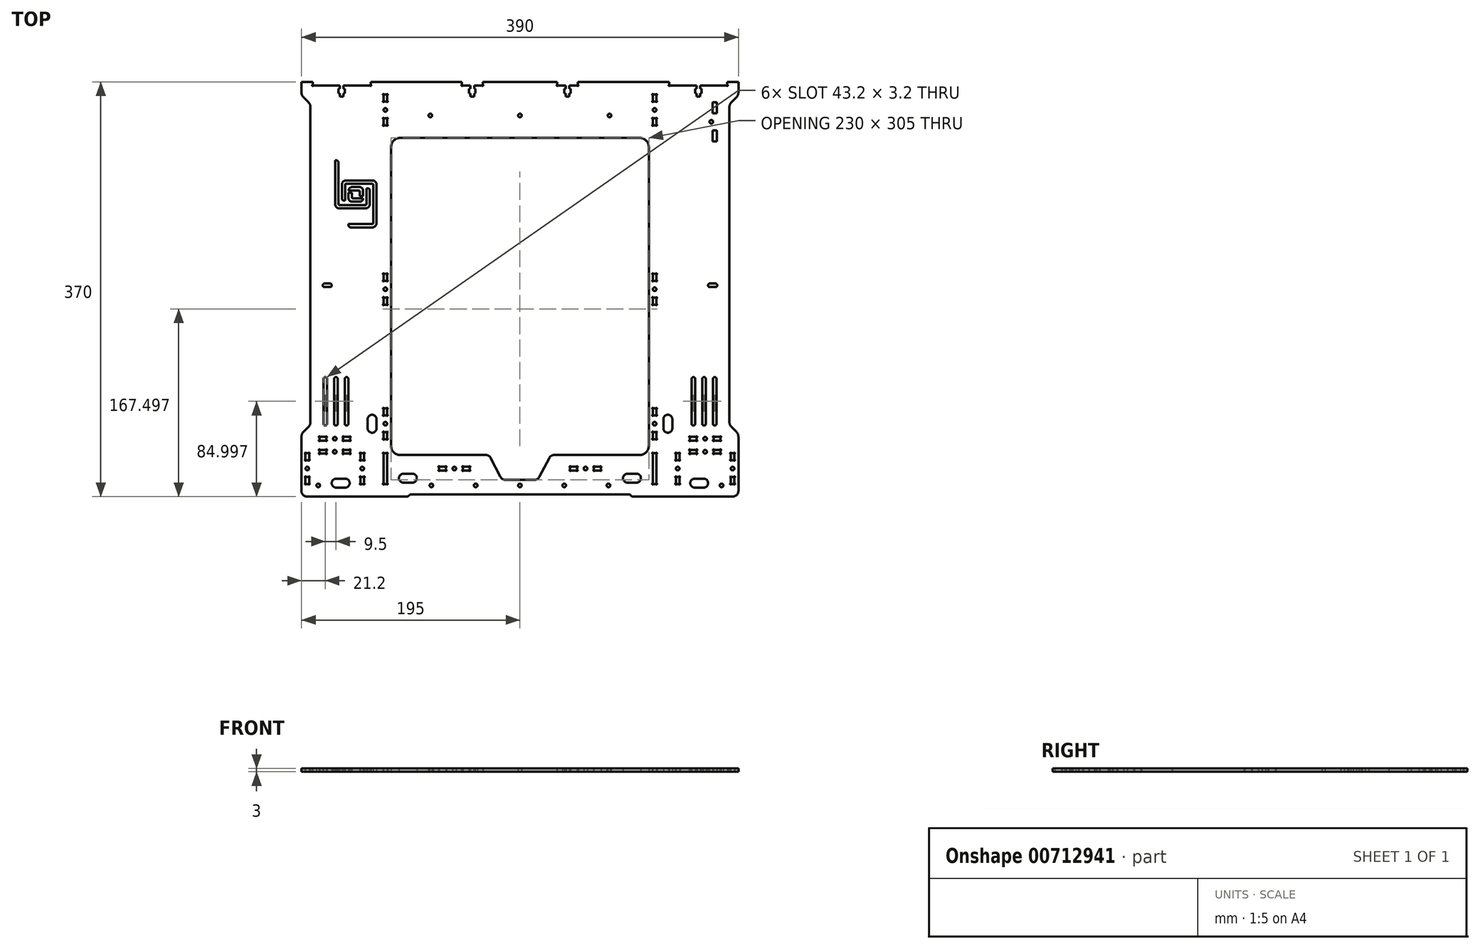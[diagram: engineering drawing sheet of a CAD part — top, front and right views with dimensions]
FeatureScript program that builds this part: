
annotation { "Feature Type Name" : "Feature", "Feature Type Description" : "" }
export const myFeature = defineFeature(function(context is Context, id is Id, definition is map)
    precondition{}
    {
        {
            var Q0;
            Q0=qCreatedBy(makeId("Top.planeOp"),FACE);
            var sketch = newSketch(context, id + "F0", { "sketchPlane" : qUnion([Q0])});
            skCircle(sketch, "E0", {"center": v(-180, -171.15) * mm, "radius": 1.6 * mm});
            skCircle(sketch, "E1", {"center": v(0, 158.85) * mm, "radius": 1.6 * mm});
            skLineSegment(sketch, "E2", {"start": v(-156, -165.15) * mm, "end": v(-164, -165.15) * mm});
            skArc(sketch, "E3", {"start": v(-156, -173.15) * mm, "mid": v(-152, -169.15) * mm, "end": v(-156, -165.15) * mm});
            skLineSegment(sketch, "E4", {"start": v(-164, -173.15) * mm, "end": v(-156, -173.15) * mm});
            skArc(sketch, "E5", {"start": v(-164, -165.15) * mm, "mid": v(-168, -169.15) * mm, "end": v(-164, -173.15) * mm});
            skLineSegment(sketch, "E6", {"start": v(156, -173.15) * mm, "end": v(164, -173.15) * mm});
            skArc(sketch, "E7", {"start": v(156, -165.15) * mm, "mid": v(152, -169.15) * mm, "end": v(156, -173.15) * mm});
            skLineSegment(sketch, "E8", {"start": v(164, -165.15) * mm, "end": v(156, -165.15) * mm});
            skArc(sketch, "E9", {"start": v(164, -173.15) * mm, "mid": v(168, -169.15) * mm, "end": v(164, -165.15) * mm});
            skLineSegment(sketch, "E10", {"start": v(-165.9, -76.15) * mm, "end": v(-165.9, -116.15) * mm});
            skArc(sketch, "E11", {"start": v(-162.7, -76.15) * mm, "mid": v(-164.3, -74.55) * mm, "end": v(-165.9, -76.15) * mm});
            skLineSegment(sketch, "E12", {"start": v(-162.7, -116.15) * mm, "end": v(-162.7, -76.15) * mm});
            skArc(sketch, "E13", {"start": v(-165.9, -116.15) * mm, "mid": v(-164.3, -117.75) * mm, "end": v(-162.7, -116.15) * mm});
            skLineSegment(sketch, "E14", {"start": v(-156.4, -76.15) * mm, "end": v(-156.4, -116.15) * mm});
            skArc(sketch, "E15", {"start": v(-153.2, -76.15) * mm, "mid": v(-154.8, -74.55) * mm, "end": v(-156.4, -76.15) * mm});
            skLineSegment(sketch, "E16", {"start": v(-153.2, -116.15) * mm, "end": v(-153.2, -76.15) * mm});
            skArc(sketch, "E17", {"start": v(-156.4, -116.15) * mm, "mid": v(-154.8, -117.75) * mm, "end": v(-153.2, -116.15) * mm});
            skLineSegment(sketch, "E18", {"start": v(-175.4, -76.15) * mm, "end": v(-175.4, -116.15) * mm});
            skArc(sketch, "E19", {"start": v(-172.2, -76.15) * mm, "mid": v(-173.8, -74.55) * mm, "end": v(-175.4, -76.15) * mm});
            skLineSegment(sketch, "E20", {"start": v(-172.2, -116.15) * mm, "end": v(-172.2, -76.15) * mm});
            skArc(sketch, "E21", {"start": v(-175.4, -116.15) * mm, "mid": v(-173.8, -117.75) * mm, "end": v(-172.2, -116.15) * mm});
            skCircle(sketch, "E22", {"center": v(170.82, 153.25) * mm, "radius": 1.6 * mm});
            skCircle(sketch, "E23", {"center": v(165.3, -141.15) * mm, "radius": 1.6 * mm});
            skLineSegment(sketch, "E24", {"start": v(-157.8, -140.37) * mm, "end": v(-157.8, -141.94) * mm});
            skArc(sketch, "E25", {"start": v(-157.8, -140.37) * mm, "mid": v(-157.87, -140.12) * mm, "end": v(-158.05, -139.94) * mm});
            skArc(sketch, "E26", {"start": v(-157.37, -139.25) * mm, "mid": v(-158.15, -139.15) * mm, "end": v(-158.05, -139.94) * mm});
            skArc(sketch, "E27", {"start": v(-157.37, -139.25) * mm, "mid": v(-157.18, -139.44) * mm, "end": v(-156.93, -139.5) * mm});
            skLineSegment(sketch, "E28", {"start": v(-152.47, -139.5) * mm, "end": v(-156.93, -139.5) * mm});
            skArc(sketch, "E29", {"start": v(-152.47, -139.5) * mm, "mid": v(-152.22, -139.44) * mm, "end": v(-152.03, -139.25) * mm});
            skArc(sketch, "E30", {"start": v(-151.35, -139.94) * mm, "mid": v(-151.25, -139.15) * mm, "end": v(-152.03, -139.25) * mm});
            skArc(sketch, "E31", {"start": v(-151.35, -139.94) * mm, "mid": v(-151.53, -140.12) * mm, "end": v(-151.6, -140.37) * mm});
            skLineSegment(sketch, "E32", {"start": v(-151.6, -141.94) * mm, "end": v(-151.6, -140.37) * mm});
            skArc(sketch, "E33", {"start": v(-151.6, -141.94) * mm, "mid": v(-151.53, -142.19) * mm, "end": v(-151.35, -142.37) * mm});
            skArc(sketch, "E34", {"start": v(-152.03, -143.05) * mm, "mid": v(-151.25, -143.16) * mm, "end": v(-151.35, -142.37) * mm});
            skArc(sketch, "E35", {"start": v(-152.03, -143.05) * mm, "mid": v(-152.22, -142.87) * mm, "end": v(-152.47, -142.8) * mm});
            skLineSegment(sketch, "E36", {"start": v(-156.93, -142.8) * mm, "end": v(-152.47, -142.8) * mm});
            skArc(sketch, "E37", {"start": v(-156.93, -142.8) * mm, "mid": v(-157.18, -142.87) * mm, "end": v(-157.37, -143.05) * mm});
            skArc(sketch, "E38", {"start": v(-158.05, -142.37) * mm, "mid": v(-158.15, -143.16) * mm, "end": v(-157.37, -143.05) * mm});
            skArc(sketch, "E39", {"start": v(-158.05, -142.37) * mm, "mid": v(-157.87, -142.19) * mm, "end": v(-157.8, -141.94) * mm});
            skLineSegment(sketch, "E40", {"start": v(-179, -140.37) * mm, "end": v(-179, -141.94) * mm});
            skArc(sketch, "E41", {"start": v(-179, -140.37) * mm, "mid": v(-179.07, -140.12) * mm, "end": v(-179.25, -139.94) * mm});
            skArc(sketch, "E42", {"start": v(-178.57, -139.25) * mm, "mid": v(-179.35, -139.15) * mm, "end": v(-179.25, -139.94) * mm});
            skArc(sketch, "E43", {"start": v(-178.57, -139.25) * mm, "mid": v(-178.38, -139.44) * mm, "end": v(-178.13, -139.5) * mm});
            skLineSegment(sketch, "E44", {"start": v(-173.67, -139.5) * mm, "end": v(-178.13, -139.5) * mm});
            skArc(sketch, "E45", {"start": v(-173.67, -139.5) * mm, "mid": v(-173.42, -139.44) * mm, "end": v(-173.23, -139.25) * mm});
            skArc(sketch, "E46", {"start": v(-172.55, -139.94) * mm, "mid": v(-172.45, -139.15) * mm, "end": v(-173.23, -139.25) * mm});
            skArc(sketch, "E47", {"start": v(-172.55, -139.94) * mm, "mid": v(-172.73, -140.12) * mm, "end": v(-172.8, -140.37) * mm});
            skLineSegment(sketch, "E48", {"start": v(-172.8, -141.94) * mm, "end": v(-172.8, -140.37) * mm});
            skArc(sketch, "E49", {"start": v(-172.8, -141.94) * mm, "mid": v(-172.73, -142.19) * mm, "end": v(-172.55, -142.37) * mm});
            skArc(sketch, "E50", {"start": v(-173.23, -143.05) * mm, "mid": v(-172.45, -143.16) * mm, "end": v(-172.55, -142.37) * mm});
            skArc(sketch, "E51", {"start": v(-173.23, -143.05) * mm, "mid": v(-173.42, -142.87) * mm, "end": v(-173.67, -142.8) * mm});
            skLineSegment(sketch, "E52", {"start": v(-178.13, -142.8) * mm, "end": v(-173.67, -142.8) * mm});
            skArc(sketch, "E53", {"start": v(-178.13, -142.8) * mm, "mid": v(-178.38, -142.87) * mm, "end": v(-178.57, -143.05) * mm});
            skArc(sketch, "E54", {"start": v(-179.25, -142.37) * mm, "mid": v(-179.35, -143.16) * mm, "end": v(-178.57, -143.05) * mm});
            skArc(sketch, "E55", {"start": v(-179.25, -142.37) * mm, "mid": v(-179.07, -142.19) * mm, "end": v(-179, -141.94) * mm});
            skLineSegment(sketch, "E56", {"start": v(-96, -160.75) * mm, "end": v(-104, -160.75) * mm});
            skArc(sketch, "E57", {"start": v(-96, -168.75) * mm, "mid": v(-92, -164.75) * mm, "end": v(-96, -160.75) * mm});
            skLineSegment(sketch, "E58", {"start": v(-104, -168.75) * mm, "end": v(-96, -168.75) * mm});
            skArc(sketch, "E59", {"start": v(-104, -160.75) * mm, "mid": v(-108, -164.75) * mm, "end": v(-104, -168.75) * mm});
            skLineSegment(sketch, "E60", {"start": v(104, -160.75) * mm, "end": v(96, -160.75) * mm});
            skArc(sketch, "E61", {"start": v(104, -168.75) * mm, "mid": v(108, -164.75) * mm, "end": v(104, -160.75) * mm});
            skLineSegment(sketch, "E62", {"start": v(96, -168.75) * mm, "end": v(104, -168.75) * mm});
            skArc(sketch, "E63", {"start": v(96, -160.75) * mm, "mid": v(92, -164.75) * mm, "end": v(96, -168.75) * mm});
            skCircle(sketch, "E64", {"center": v(-79.02, -171.15) * mm, "radius": 1.6 * mm});
            skCircle(sketch, "E65", {"center": v(39.5, -171.15) * mm, "radius": 1.6 * mm});
            skCircle(sketch, "E66", {"center": v(58.53, -156.15) * mm, "radius": 1.6 * mm});
            skLineSegment(sketch, "E67", {"start": v(-51.03, -155.37) * mm, "end": v(-51.03, -156.94) * mm});
            skArc(sketch, "E68", {"start": v(-51.03, -155.37) * mm, "mid": v(-51.1, -155.12) * mm, "end": v(-51.28, -154.94) * mm});
            skArc(sketch, "E69", {"start": v(-50.6, -154.25) * mm, "mid": v(-51.38, -154.15) * mm, "end": v(-51.28, -154.94) * mm});
            skArc(sketch, "E70", {"start": v(-50.6, -154.25) * mm, "mid": v(-50.4, -154.44) * mm, "end": v(-50.16, -154.5) * mm});
            skLineSegment(sketch, "E71", {"start": v(-45.7, -154.5) * mm, "end": v(-50.16, -154.5) * mm});
            skArc(sketch, "E72", {"start": v(-45.7, -154.5) * mm, "mid": v(-45.44, -154.44) * mm, "end": v(-45.26, -154.25) * mm});
            skArc(sketch, "E73", {"start": v(-44.58, -154.94) * mm, "mid": v(-44.47, -154.15) * mm, "end": v(-45.26, -154.25) * mm});
            skArc(sketch, "E74", {"start": v(-44.58, -154.94) * mm, "mid": v(-44.76, -155.12) * mm, "end": v(-44.83, -155.37) * mm});
            skLineSegment(sketch, "E75", {"start": v(-44.83, -156.94) * mm, "end": v(-44.83, -155.37) * mm});
            skArc(sketch, "E76", {"start": v(-44.83, -156.94) * mm, "mid": v(-44.76, -157.19) * mm, "end": v(-44.58, -157.37) * mm});
            skArc(sketch, "E77", {"start": v(-45.26, -158.05) * mm, "mid": v(-44.47, -158.16) * mm, "end": v(-44.58, -157.37) * mm});
            skArc(sketch, "E78", {"start": v(-45.26, -158.05) * mm, "mid": v(-45.44, -157.87) * mm, "end": v(-45.7, -157.8) * mm});
            skLineSegment(sketch, "E79", {"start": v(-50.16, -157.8) * mm, "end": v(-45.7, -157.8) * mm});
            skArc(sketch, "E80", {"start": v(-50.16, -157.8) * mm, "mid": v(-50.4, -157.87) * mm, "end": v(-50.6, -158.05) * mm});
            skArc(sketch, "E81", {"start": v(-51.28, -157.37) * mm, "mid": v(-51.38, -158.16) * mm, "end": v(-50.6, -158.05) * mm});
            skArc(sketch, "E82", {"start": v(-51.28, -157.37) * mm, "mid": v(-51.1, -157.19) * mm, "end": v(-51.03, -156.94) * mm});
            skLineSegment(sketch, "E83", {"start": v(-72.23, -155.37) * mm, "end": v(-72.23, -156.94) * mm});
            skArc(sketch, "E84", {"start": v(-72.23, -155.37) * mm, "mid": v(-72.3, -155.12) * mm, "end": v(-72.48, -154.94) * mm});
            skArc(sketch, "E85", {"start": v(-71.8, -154.25) * mm, "mid": v(-72.58, -154.15) * mm, "end": v(-72.48, -154.94) * mm});
            skArc(sketch, "E86", {"start": v(-71.8, -154.25) * mm, "mid": v(-71.6, -154.44) * mm, "end": v(-71.36, -154.5) * mm});
            skLineSegment(sketch, "E87", {"start": v(-66.9, -154.5) * mm, "end": v(-71.36, -154.5) * mm});
            skArc(sketch, "E88", {"start": v(-66.9, -154.5) * mm, "mid": v(-66.64, -154.44) * mm, "end": v(-66.46, -154.25) * mm});
            skArc(sketch, "E89", {"start": v(-65.78, -154.94) * mm, "mid": v(-65.67, -154.15) * mm, "end": v(-66.46, -154.25) * mm});
            skArc(sketch, "E90", {"start": v(-65.78, -154.94) * mm, "mid": v(-65.96, -155.12) * mm, "end": v(-66.03, -155.37) * mm});
            skLineSegment(sketch, "E91", {"start": v(-66.03, -156.94) * mm, "end": v(-66.03, -155.37) * mm});
            skArc(sketch, "E92", {"start": v(-66.03, -156.94) * mm, "mid": v(-65.96, -157.19) * mm, "end": v(-65.78, -157.37) * mm});
            skArc(sketch, "E93", {"start": v(-66.46, -158.05) * mm, "mid": v(-65.67, -158.16) * mm, "end": v(-65.78, -157.37) * mm});
            skArc(sketch, "E94", {"start": v(-66.46, -158.05) * mm, "mid": v(-66.64, -157.87) * mm, "end": v(-66.9, -157.8) * mm});
            skLineSegment(sketch, "E95", {"start": v(-71.36, -157.8) * mm, "end": v(-66.9, -157.8) * mm});
            skArc(sketch, "E96", {"start": v(-71.36, -157.8) * mm, "mid": v(-71.6, -157.87) * mm, "end": v(-71.8, -158.05) * mm});
            skArc(sketch, "E97", {"start": v(-72.48, -157.37) * mm, "mid": v(-72.58, -158.16) * mm, "end": v(-71.8, -158.05) * mm});
            skArc(sketch, "E98", {"start": v(-72.48, -157.37) * mm, "mid": v(-72.3, -157.19) * mm, "end": v(-72.23, -156.94) * mm});
            skCircle(sketch, "E99", {"center": v(189.82, -156.15) * mm, "radius": 1.6 * mm});
            skCircle(sketch, "E100", {"center": v(140.78, -156.15) * mm, "radius": 1.6 * mm});
            skCircle(sketch, "E101", {"center": v(120.17, 3.85) * mm, "radius": 1.6 * mm});
            skCircle(sketch, "E102", {"center": v(-120.18, 163.85) * mm, "radius": 1.6 * mm});
            skCircle(sketch, "E103", {"center": v(-120.17, -116.15) * mm, "radius": 1.6 * mm});
            skCircle(sketch, "E104", {"center": v(-165.3, -129.5) * mm, "radius": 1.6 * mm});
            skArc(sketch, "E105", {"start": v(188.17, -143.32) * mm, "mid": v(188.1, -143.07) * mm, "end": v(187.92, -142.89) * mm});
            skArc(sketch, "E106", {"start": v(188.6, -142.2) * mm, "mid": v(187.82, -142.1) * mm, "end": v(187.92, -142.89) * mm});
            skArc(sketch, "E107", {"start": v(188.6, -142.2) * mm, "mid": v(188.79, -142.39) * mm, "end": v(189.04, -142.45) * mm});
            skLineSegment(sketch, "E108", {"start": v(190.6, -142.45) * mm, "end": v(189.04, -142.45) * mm});
            skArc(sketch, "E109", {"start": v(190.6, -142.45) * mm, "mid": v(190.85, -142.39) * mm, "end": v(191.04, -142.2) * mm});
            skArc(sketch, "E110", {"start": v(191.72, -142.89) * mm, "mid": v(191.82, -142.1) * mm, "end": v(191.04, -142.2) * mm});
            skArc(sketch, "E111", {"start": v(191.72, -142.89) * mm, "mid": v(191.54, -143.07) * mm, "end": v(191.47, -143.32) * mm});
            skLineSegment(sketch, "E112", {"start": v(191.47, -147.79) * mm, "end": v(191.47, -143.32) * mm});
            skArc(sketch, "E113", {"start": v(191.47, -147.79) * mm, "mid": v(191.54, -148.04) * mm, "end": v(191.72, -148.22) * mm});
            skArc(sketch, "E114", {"start": v(191.04, -148.9) * mm, "mid": v(191.82, -149) * mm, "end": v(191.72, -148.22) * mm});
            skArc(sketch, "E115", {"start": v(191.04, -148.9) * mm, "mid": v(190.85, -148.72) * mm, "end": v(190.6, -148.65) * mm});
            skLineSegment(sketch, "E116", {"start": v(189.04, -148.65) * mm, "end": v(190.6, -148.65) * mm});
            skArc(sketch, "E117", {"start": v(189.04, -148.65) * mm, "mid": v(188.79, -148.72) * mm, "end": v(188.6, -148.9) * mm});
            skArc(sketch, "E118", {"start": v(187.92, -148.22) * mm, "mid": v(187.82, -149) * mm, "end": v(188.6, -148.9) * mm});
            skArc(sketch, "E119", {"start": v(187.92, -148.22) * mm, "mid": v(188.1, -148.04) * mm, "end": v(188.17, -147.79) * mm});
            skLineSegment(sketch, "E120", {"start": v(188.17, -143.32) * mm, "end": v(188.17, -147.79) * mm});
            skArc(sketch, "E121", {"start": v(188.17, -164.52) * mm, "mid": v(188.1, -164.27) * mm, "end": v(187.92, -164.09) * mm});
            skArc(sketch, "E122", {"start": v(188.6, -163.4) * mm, "mid": v(187.82, -163.3) * mm, "end": v(187.92, -164.09) * mm});
            skArc(sketch, "E123", {"start": v(188.6, -163.4) * mm, "mid": v(188.79, -163.59) * mm, "end": v(189.04, -163.65) * mm});
            skLineSegment(sketch, "E124", {"start": v(190.6, -163.65) * mm, "end": v(189.04, -163.65) * mm});
            skArc(sketch, "E125", {"start": v(190.6, -163.65) * mm, "mid": v(190.85, -163.59) * mm, "end": v(191.04, -163.4) * mm});
            skArc(sketch, "E126", {"start": v(191.72, -164.09) * mm, "mid": v(191.82, -163.3) * mm, "end": v(191.04, -163.4) * mm});
            skArc(sketch, "E127", {"start": v(191.72, -164.09) * mm, "mid": v(191.54, -164.27) * mm, "end": v(191.47, -164.52) * mm});
            skLineSegment(sketch, "E128", {"start": v(191.47, -168.99) * mm, "end": v(191.47, -164.52) * mm});
            skArc(sketch, "E129", {"start": v(191.47, -168.99) * mm, "mid": v(191.54, -169.24) * mm, "end": v(191.72, -169.42) * mm});
            skArc(sketch, "E130", {"start": v(191.04, -170.1) * mm, "mid": v(191.82, -170.2) * mm, "end": v(191.72, -169.42) * mm});
            skArc(sketch, "E131", {"start": v(191.04, -170.1) * mm, "mid": v(190.85, -169.92) * mm, "end": v(190.6, -169.85) * mm});
            skLineSegment(sketch, "E132", {"start": v(189.04, -169.85) * mm, "end": v(190.6, -169.85) * mm});
            skArc(sketch, "E133", {"start": v(189.04, -169.85) * mm, "mid": v(188.79, -169.92) * mm, "end": v(188.6, -170.1) * mm});
            skArc(sketch, "E134", {"start": v(187.92, -169.42) * mm, "mid": v(187.82, -170.2) * mm, "end": v(188.6, -170.1) * mm});
            skArc(sketch, "E135", {"start": v(187.92, -169.42) * mm, "mid": v(188.1, -169.24) * mm, "end": v(188.17, -168.99) * mm});
            skLineSegment(sketch, "E136", {"start": v(188.17, -164.52) * mm, "end": v(188.17, -168.99) * mm});
            skArc(sketch, "E137", {"start": v(178.13, -127.86) * mm, "mid": v(178.38, -127.8) * mm, "end": v(178.57, -127.6) * mm});
            skArc(sketch, "E138", {"start": v(179.25, -128.3) * mm, "mid": v(179.35, -127.5) * mm, "end": v(178.57, -127.6) * mm});
            skArc(sketch, "E139", {"start": v(179.25, -128.3) * mm, "mid": v(179.07, -128.47) * mm, "end": v(179, -128.72) * mm});
            skLineSegment(sketch, "E140", {"start": v(179, -130.3) * mm, "end": v(179, -128.72) * mm});
            skArc(sketch, "E141", {"start": v(179, -130.3) * mm, "mid": v(179.07, -130.54) * mm, "end": v(179.25, -130.72) * mm});
            skArc(sketch, "E142", {"start": v(178.57, -131.4) * mm, "mid": v(179.35, -131.51) * mm, "end": v(179.25, -130.72) * mm});
            skArc(sketch, "E143", {"start": v(178.57, -131.4) * mm, "mid": v(178.38, -131.22) * mm, "end": v(178.13, -131.16) * mm});
            skLineSegment(sketch, "E144", {"start": v(173.67, -131.16) * mm, "end": v(178.13, -131.16) * mm});
            skArc(sketch, "E145", {"start": v(173.67, -131.16) * mm, "mid": v(173.42, -131.22) * mm, "end": v(173.23, -131.4) * mm});
            skArc(sketch, "E146", {"start": v(172.55, -130.72) * mm, "mid": v(172.45, -131.51) * mm, "end": v(173.23, -131.4) * mm});
            skArc(sketch, "E147", {"start": v(172.55, -130.72) * mm, "mid": v(172.73, -130.54) * mm, "end": v(172.8, -130.3) * mm});
            skLineSegment(sketch, "E148", {"start": v(172.8, -128.72) * mm, "end": v(172.8, -130.3) * mm});
            skArc(sketch, "E149", {"start": v(172.8, -128.72) * mm, "mid": v(172.73, -128.47) * mm, "end": v(172.55, -128.3) * mm});
            skArc(sketch, "E150", {"start": v(173.23, -127.6) * mm, "mid": v(172.45, -127.5) * mm, "end": v(172.55, -128.3) * mm});
            skArc(sketch, "E151", {"start": v(173.23, -127.6) * mm, "mid": v(173.42, -127.8) * mm, "end": v(173.67, -127.86) * mm});
            skLineSegment(sketch, "E152", {"start": v(178.13, -127.86) * mm, "end": v(173.67, -127.86) * mm});
            skArc(sketch, "E153", {"start": v(156.93, -127.86) * mm, "mid": v(157.18, -127.8) * mm, "end": v(157.37, -127.6) * mm});
            skArc(sketch, "E154", {"start": v(158.05, -128.3) * mm, "mid": v(158.15, -127.5) * mm, "end": v(157.37, -127.6) * mm});
            skArc(sketch, "E155", {"start": v(158.05, -128.3) * mm, "mid": v(157.87, -128.47) * mm, "end": v(157.8, -128.72) * mm});
            skLineSegment(sketch, "E156", {"start": v(157.8, -130.3) * mm, "end": v(157.8, -128.72) * mm});
            skArc(sketch, "E157", {"start": v(157.8, -130.3) * mm, "mid": v(157.87, -130.54) * mm, "end": v(158.05, -130.72) * mm});
            skArc(sketch, "E158", {"start": v(157.37, -131.4) * mm, "mid": v(158.15, -131.51) * mm, "end": v(158.05, -130.72) * mm});
            skArc(sketch, "E159", {"start": v(157.37, -131.4) * mm, "mid": v(157.18, -131.22) * mm, "end": v(156.93, -131.16) * mm});
            skLineSegment(sketch, "E160", {"start": v(152.47, -131.16) * mm, "end": v(156.93, -131.16) * mm});
            skArc(sketch, "E161", {"start": v(152.47, -131.16) * mm, "mid": v(152.22, -131.22) * mm, "end": v(152.03, -131.4) * mm});
            skArc(sketch, "E162", {"start": v(151.35, -130.72) * mm, "mid": v(151.25, -131.51) * mm, "end": v(152.03, -131.4) * mm});
            skArc(sketch, "E163", {"start": v(151.35, -130.72) * mm, "mid": v(151.53, -130.54) * mm, "end": v(151.6, -130.3) * mm});
            skLineSegment(sketch, "E164", {"start": v(151.6, -128.72) * mm, "end": v(151.6, -130.3) * mm});
            skArc(sketch, "E165", {"start": v(151.6, -128.72) * mm, "mid": v(151.53, -128.47) * mm, "end": v(151.35, -128.3) * mm});
            skArc(sketch, "E166", {"start": v(152.03, -127.6) * mm, "mid": v(151.25, -127.5) * mm, "end": v(151.35, -128.3) * mm});
            skArc(sketch, "E167", {"start": v(152.03, -127.6) * mm, "mid": v(152.22, -127.8) * mm, "end": v(152.47, -127.86) * mm});
            skLineSegment(sketch, "E168", {"start": v(156.93, -127.86) * mm, "end": v(152.47, -127.86) * mm});
            skArc(sketch, "E169", {"start": v(139.13, -143.32) * mm, "mid": v(139.06, -143.07) * mm, "end": v(138.88, -142.89) * mm});
            skArc(sketch, "E170", {"start": v(139.56, -142.2) * mm, "mid": v(138.78, -142.1) * mm, "end": v(138.88, -142.89) * mm});
            skArc(sketch, "E171", {"start": v(139.56, -142.2) * mm, "mid": v(139.75, -142.39) * mm, "end": v(140, -142.45) * mm});
            skLineSegment(sketch, "E172", {"start": v(141.56, -142.45) * mm, "end": v(140, -142.45) * mm});
            skArc(sketch, "E173", {"start": v(141.56, -142.45) * mm, "mid": v(141.81, -142.39) * mm, "end": v(142, -142.2) * mm});
            skArc(sketch, "E174", {"start": v(142.68, -142.89) * mm, "mid": v(142.78, -142.1) * mm, "end": v(142, -142.2) * mm});
            skArc(sketch, "E175", {"start": v(142.68, -142.89) * mm, "mid": v(142.5, -143.07) * mm, "end": v(142.43, -143.32) * mm});
            skLineSegment(sketch, "E176", {"start": v(142.43, -147.79) * mm, "end": v(142.43, -143.32) * mm});
            skArc(sketch, "E177", {"start": v(142.43, -147.79) * mm, "mid": v(142.5, -148.04) * mm, "end": v(142.68, -148.22) * mm});
            skArc(sketch, "E178", {"start": v(142, -148.9) * mm, "mid": v(142.78, -149) * mm, "end": v(142.68, -148.22) * mm});
            skArc(sketch, "E179", {"start": v(142, -148.9) * mm, "mid": v(141.81, -148.72) * mm, "end": v(141.56, -148.65) * mm});
            skLineSegment(sketch, "E180", {"start": v(140, -148.65) * mm, "end": v(141.56, -148.65) * mm});
            skArc(sketch, "E181", {"start": v(140, -148.65) * mm, "mid": v(139.75, -148.72) * mm, "end": v(139.56, -148.9) * mm});
            skArc(sketch, "E182", {"start": v(138.88, -148.22) * mm, "mid": v(138.78, -149) * mm, "end": v(139.56, -148.9) * mm});
            skArc(sketch, "E183", {"start": v(138.88, -148.22) * mm, "mid": v(139.06, -148.04) * mm, "end": v(139.13, -147.79) * mm});
            skLineSegment(sketch, "E184", {"start": v(139.13, -143.32) * mm, "end": v(139.13, -147.79) * mm});
            skArc(sketch, "E185", {"start": v(139.13, -164.52) * mm, "mid": v(139.06, -164.27) * mm, "end": v(138.88, -164.09) * mm});
            skArc(sketch, "E186", {"start": v(139.56, -163.4) * mm, "mid": v(138.78, -163.3) * mm, "end": v(138.88, -164.09) * mm});
            skArc(sketch, "E187", {"start": v(139.56, -163.4) * mm, "mid": v(139.75, -163.59) * mm, "end": v(140, -163.65) * mm});
            skLineSegment(sketch, "E188", {"start": v(141.56, -163.65) * mm, "end": v(140, -163.65) * mm});
            skArc(sketch, "E189", {"start": v(141.56, -163.65) * mm, "mid": v(141.81, -163.59) * mm, "end": v(142, -163.4) * mm});
            skArc(sketch, "E190", {"start": v(142.68, -164.09) * mm, "mid": v(142.78, -163.3) * mm, "end": v(142, -163.4) * mm});
            skArc(sketch, "E191", {"start": v(142.68, -164.09) * mm, "mid": v(142.5, -164.27) * mm, "end": v(142.43, -164.52) * mm});
            skLineSegment(sketch, "E192", {"start": v(142.43, -168.99) * mm, "end": v(142.43, -164.52) * mm});
            skArc(sketch, "E193", {"start": v(142.43, -168.99) * mm, "mid": v(142.5, -169.24) * mm, "end": v(142.68, -169.42) * mm});
            skArc(sketch, "E194", {"start": v(142, -170.1) * mm, "mid": v(142.78, -170.2) * mm, "end": v(142.68, -169.42) * mm});
            skArc(sketch, "E195", {"start": v(142, -170.1) * mm, "mid": v(141.81, -169.92) * mm, "end": v(141.56, -169.85) * mm});
            skLineSegment(sketch, "E196", {"start": v(140, -169.85) * mm, "end": v(141.56, -169.85) * mm});
            skArc(sketch, "E197", {"start": v(140, -169.85) * mm, "mid": v(139.75, -169.92) * mm, "end": v(139.56, -170.1) * mm});
            skArc(sketch, "E198", {"start": v(138.88, -169.42) * mm, "mid": v(138.78, -170.2) * mm, "end": v(139.56, -170.1) * mm});
            skArc(sketch, "E199", {"start": v(138.88, -169.42) * mm, "mid": v(139.06, -169.24) * mm, "end": v(139.13, -168.99) * mm});
            skLineSegment(sketch, "E200", {"start": v(139.13, -164.52) * mm, "end": v(139.13, -168.99) * mm});
            skLineSegment(sketch, "E201", {"start": v(120.96, 177.55) * mm, "end": v(119.4, 177.55) * mm});
            skArc(sketch, "E202", {"start": v(120.96, 177.55) * mm, "mid": v(121.2, 177.61) * mm, "end": v(121.4, 177.8) * mm});
            skArc(sketch, "E203", {"start": v(122.07, 177.11) * mm, "mid": v(122.18, 177.9) * mm, "end": v(121.4, 177.8) * mm});
            skArc(sketch, "E204", {"start": v(122.07, 177.11) * mm, "mid": v(121.9, 176.93) * mm, "end": v(121.82, 176.68) * mm});
            skLineSegment(sketch, "E205", {"start": v(121.82, 172.21) * mm, "end": v(121.82, 176.68) * mm});
            skArc(sketch, "E206", {"start": v(121.82, 172.21) * mm, "mid": v(121.9, 171.96) * mm, "end": v(122.07, 171.78) * mm});
            skArc(sketch, "E207", {"start": v(121.4, 171.1) * mm, "mid": v(122.18, 171) * mm, "end": v(122.07, 171.78) * mm});
            skArc(sketch, "E208", {"start": v(121.4, 171.1) * mm, "mid": v(121.2, 171.28) * mm, "end": v(120.96, 171.35) * mm});
            skLineSegment(sketch, "E209", {"start": v(119.4, 171.35) * mm, "end": v(120.96, 171.35) * mm});
            skArc(sketch, "E210", {"start": v(119.4, 171.35) * mm, "mid": v(119.14, 171.28) * mm, "end": v(118.96, 171.1) * mm});
            skArc(sketch, "E211", {"start": v(118.28, 171.78) * mm, "mid": v(118.17, 171) * mm, "end": v(118.96, 171.1) * mm});
            skArc(sketch, "E212", {"start": v(118.28, 171.78) * mm, "mid": v(118.46, 171.96) * mm, "end": v(118.53, 172.21) * mm});
            skLineSegment(sketch, "E213", {"start": v(118.53, 176.68) * mm, "end": v(118.53, 172.21) * mm});
            skArc(sketch, "E214", {"start": v(118.53, 176.68) * mm, "mid": v(118.46, 176.93) * mm, "end": v(118.28, 177.11) * mm});
            skArc(sketch, "E215", {"start": v(118.96, 177.8) * mm, "mid": v(118.17, 177.9) * mm, "end": v(118.28, 177.11) * mm});
            skArc(sketch, "E216", {"start": v(118.96, 177.8) * mm, "mid": v(119.14, 177.61) * mm, "end": v(119.4, 177.55) * mm});
            skLineSegment(sketch, "E217", {"start": v(120.96, 156.35) * mm, "end": v(119.4, 156.35) * mm});
            skArc(sketch, "E218", {"start": v(120.96, 156.35) * mm, "mid": v(121.2, 156.41) * mm, "end": v(121.4, 156.6) * mm});
            skArc(sketch, "E219", {"start": v(122.07, 155.91) * mm, "mid": v(122.18, 156.7) * mm, "end": v(121.4, 156.6) * mm});
            skArc(sketch, "E220", {"start": v(122.07, 155.91) * mm, "mid": v(121.9, 155.73) * mm, "end": v(121.82, 155.48) * mm});
            skLineSegment(sketch, "E221", {"start": v(121.82, 151.01) * mm, "end": v(121.82, 155.48) * mm});
            skArc(sketch, "E222", {"start": v(121.82, 151.01) * mm, "mid": v(121.9, 150.76) * mm, "end": v(122.07, 150.58) * mm});
            skArc(sketch, "E223", {"start": v(121.4, 149.9) * mm, "mid": v(122.18, 149.8) * mm, "end": v(122.07, 150.58) * mm});
            skArc(sketch, "E224", {"start": v(121.4, 149.9) * mm, "mid": v(121.2, 150.08) * mm, "end": v(120.96, 150.15) * mm});
            skLineSegment(sketch, "E225", {"start": v(119.4, 150.15) * mm, "end": v(120.96, 150.15) * mm});
            skArc(sketch, "E226", {"start": v(119.4, 150.15) * mm, "mid": v(119.14, 150.08) * mm, "end": v(118.96, 149.9) * mm});
            skArc(sketch, "E227", {"start": v(118.28, 150.58) * mm, "mid": v(118.17, 149.8) * mm, "end": v(118.96, 149.9) * mm});
            skArc(sketch, "E228", {"start": v(118.28, 150.58) * mm, "mid": v(118.46, 150.76) * mm, "end": v(118.53, 151.01) * mm});
            skLineSegment(sketch, "E229", {"start": v(118.53, 155.48) * mm, "end": v(118.53, 151.01) * mm});
            skArc(sketch, "E230", {"start": v(118.53, 155.48) * mm, "mid": v(118.46, 155.73) * mm, "end": v(118.28, 155.91) * mm});
            skArc(sketch, "E231", {"start": v(118.96, 156.6) * mm, "mid": v(118.17, 156.7) * mm, "end": v(118.28, 155.91) * mm});
            skArc(sketch, "E232", {"start": v(118.96, 156.6) * mm, "mid": v(119.14, 156.41) * mm, "end": v(119.4, 156.35) * mm});
            skLineSegment(sketch, "E233", {"start": v(120.96, 17.55) * mm, "end": v(119.4, 17.55) * mm});
            skArc(sketch, "E234", {"start": v(120.96, 17.55) * mm, "mid": v(121.2, 17.61) * mm, "end": v(121.4, 17.8) * mm});
            skArc(sketch, "E235", {"start": v(122.07, 17.11) * mm, "mid": v(122.18, 17.9) * mm, "end": v(121.4, 17.8) * mm});
            skArc(sketch, "E236", {"start": v(122.07, 17.11) * mm, "mid": v(121.9, 16.93) * mm, "end": v(121.82, 16.68) * mm});
            skLineSegment(sketch, "E237", {"start": v(121.82, 12.21) * mm, "end": v(121.82, 16.68) * mm});
            skArc(sketch, "E238", {"start": v(121.82, 12.21) * mm, "mid": v(121.9, 11.96) * mm, "end": v(122.07, 11.78) * mm});
            skArc(sketch, "E239", {"start": v(121.4, 11.1) * mm, "mid": v(122.18, 11) * mm, "end": v(122.07, 11.78) * mm});
            skArc(sketch, "E240", {"start": v(121.4, 11.1) * mm, "mid": v(121.2, 11.28) * mm, "end": v(120.96, 11.35) * mm});
            skLineSegment(sketch, "E241", {"start": v(119.4, 11.35) * mm, "end": v(120.96, 11.35) * mm});
            skArc(sketch, "E242", {"start": v(119.4, 11.35) * mm, "mid": v(119.14, 11.28) * mm, "end": v(118.96, 11.1) * mm});
            skArc(sketch, "E243", {"start": v(118.28, 11.78) * mm, "mid": v(118.17, 11) * mm, "end": v(118.96, 11.1) * mm});
            skArc(sketch, "E244", {"start": v(118.28, 11.78) * mm, "mid": v(118.46, 11.96) * mm, "end": v(118.53, 12.21) * mm});
            skLineSegment(sketch, "E245", {"start": v(118.53, 16.68) * mm, "end": v(118.53, 12.21) * mm});
            skArc(sketch, "E246", {"start": v(118.53, 16.68) * mm, "mid": v(118.46, 16.93) * mm, "end": v(118.28, 17.11) * mm});
            skArc(sketch, "E247", {"start": v(118.96, 17.8) * mm, "mid": v(118.17, 17.9) * mm, "end": v(118.28, 17.11) * mm});
            skArc(sketch, "E248", {"start": v(118.96, 17.8) * mm, "mid": v(119.14, 17.61) * mm, "end": v(119.4, 17.55) * mm});
            skLineSegment(sketch, "E249", {"start": v(120.96, -3.65) * mm, "end": v(119.4, -3.65) * mm});
            skArc(sketch, "E250", {"start": v(120.96, -3.65) * mm, "mid": v(121.2, -3.59) * mm, "end": v(121.4, -3.4) * mm});
            skArc(sketch, "E251", {"start": v(122.07, -4.09) * mm, "mid": v(122.18, -3.3) * mm, "end": v(121.4, -3.4) * mm});
            skArc(sketch, "E252", {"start": v(122.07, -4.09) * mm, "mid": v(121.9, -4.27) * mm, "end": v(121.82, -4.52) * mm});
            skLineSegment(sketch, "E253", {"start": v(121.82, -8.99) * mm, "end": v(121.82, -4.52) * mm});
            skArc(sketch, "E254", {"start": v(121.82, -8.99) * mm, "mid": v(121.9, -9.24) * mm, "end": v(122.07, -9.42) * mm});
            skArc(sketch, "E255", {"start": v(121.4, -10.1) * mm, "mid": v(122.18, -10.2) * mm, "end": v(122.07, -9.42) * mm});
            skArc(sketch, "E256", {"start": v(121.4, -10.1) * mm, "mid": v(121.2, -9.92) * mm, "end": v(120.96, -9.85) * mm});
            skLineSegment(sketch, "E257", {"start": v(119.4, -9.85) * mm, "end": v(120.96, -9.85) * mm});
            skArc(sketch, "E258", {"start": v(119.4, -9.85) * mm, "mid": v(119.14, -9.92) * mm, "end": v(118.96, -10.1) * mm});
            skArc(sketch, "E259", {"start": v(118.28, -9.42) * mm, "mid": v(118.17, -10.2) * mm, "end": v(118.96, -10.1) * mm});
            skArc(sketch, "E260", {"start": v(118.28, -9.42) * mm, "mid": v(118.46, -9.24) * mm, "end": v(118.53, -8.99) * mm});
            skLineSegment(sketch, "E261", {"start": v(118.53, -4.52) * mm, "end": v(118.53, -8.99) * mm});
            skArc(sketch, "E262", {"start": v(118.53, -4.52) * mm, "mid": v(118.46, -4.27) * mm, "end": v(118.28, -4.09) * mm});
            skArc(sketch, "E263", {"start": v(118.96, -3.4) * mm, "mid": v(118.17, -3.3) * mm, "end": v(118.28, -4.09) * mm});
            skArc(sketch, "E264", {"start": v(118.96, -3.4) * mm, "mid": v(119.14, -3.59) * mm, "end": v(119.4, -3.65) * mm});
            skArc(sketch, "E265", {"start": v(118.53, -103.32) * mm, "mid": v(118.46, -103.07) * mm, "end": v(118.28, -102.89) * mm});
            skArc(sketch, "E266", {"start": v(118.96, -102.2) * mm, "mid": v(118.17, -102.1) * mm, "end": v(118.28, -102.89) * mm});
            skArc(sketch, "E267", {"start": v(118.96, -102.2) * mm, "mid": v(119.14, -102.39) * mm, "end": v(119.4, -102.45) * mm});
            skLineSegment(sketch, "E268", {"start": v(120.96, -102.45) * mm, "end": v(119.4, -102.45) * mm});
            skArc(sketch, "E269", {"start": v(120.96, -102.45) * mm, "mid": v(121.2, -102.39) * mm, "end": v(121.4, -102.2) * mm});
            skArc(sketch, "E270", {"start": v(122.07, -102.89) * mm, "mid": v(122.18, -102.1) * mm, "end": v(121.4, -102.2) * mm});
            skArc(sketch, "E271", {"start": v(122.07, -102.89) * mm, "mid": v(121.9, -103.07) * mm, "end": v(121.83, -103.32) * mm});
            skLineSegment(sketch, "E272", {"start": v(121.83, -107.79) * mm, "end": v(121.83, -103.32) * mm});
            skArc(sketch, "E273", {"start": v(121.83, -107.79) * mm, "mid": v(121.9, -108.04) * mm, "end": v(122.08, -108.22) * mm});
            skArc(sketch, "E274", {"start": v(121.4, -108.9) * mm, "mid": v(122.18, -109) * mm, "end": v(122.08, -108.22) * mm});
            skArc(sketch, "E275", {"start": v(121.4, -108.9) * mm, "mid": v(121.2, -108.72) * mm, "end": v(120.96, -108.65) * mm});
            skLineSegment(sketch, "E276", {"start": v(119.4, -108.65) * mm, "end": v(120.96, -108.65) * mm});
            skArc(sketch, "E277", {"start": v(119.4, -108.65) * mm, "mid": v(119.14, -108.72) * mm, "end": v(118.96, -108.9) * mm});
            skArc(sketch, "E278", {"start": v(118.28, -108.22) * mm, "mid": v(118.17, -109) * mm, "end": v(118.96, -108.9) * mm});
            skArc(sketch, "E279", {"start": v(118.28, -108.22) * mm, "mid": v(118.46, -108.04) * mm, "end": v(118.53, -107.79) * mm});
            skLineSegment(sketch, "E280", {"start": v(118.53, -103.32) * mm, "end": v(118.53, -107.79) * mm});
            skArc(sketch, "E281", {"start": v(118.53, -124.52) * mm, "mid": v(118.46, -124.27) * mm, "end": v(118.28, -124.09) * mm});
            skArc(sketch, "E282", {"start": v(118.96, -123.4) * mm, "mid": v(118.17, -123.3) * mm, "end": v(118.28, -124.09) * mm});
            skArc(sketch, "E283", {"start": v(118.96, -123.4) * mm, "mid": v(119.14, -123.59) * mm, "end": v(119.4, -123.65) * mm});
            skLineSegment(sketch, "E284", {"start": v(120.96, -123.65) * mm, "end": v(119.4, -123.65) * mm});
            skArc(sketch, "E285", {"start": v(120.96, -123.65) * mm, "mid": v(121.2, -123.59) * mm, "end": v(121.4, -123.4) * mm});
            skArc(sketch, "E286", {"start": v(122.07, -124.09) * mm, "mid": v(122.18, -123.3) * mm, "end": v(121.4, -123.4) * mm});
            skArc(sketch, "E287", {"start": v(122.07, -124.09) * mm, "mid": v(121.9, -124.27) * mm, "end": v(121.83, -124.52) * mm});
            skLineSegment(sketch, "E288", {"start": v(121.83, -128.99) * mm, "end": v(121.83, -124.52) * mm});
            skArc(sketch, "E289", {"start": v(121.83, -128.99) * mm, "mid": v(121.9, -129.24) * mm, "end": v(122.08, -129.42) * mm});
            skArc(sketch, "E290", {"start": v(121.4, -130.1) * mm, "mid": v(122.18, -130.2) * mm, "end": v(122.08, -129.42) * mm});
            skArc(sketch, "E291", {"start": v(121.4, -130.1) * mm, "mid": v(121.2, -129.92) * mm, "end": v(120.96, -129.85) * mm});
            skLineSegment(sketch, "E292", {"start": v(119.4, -129.85) * mm, "end": v(120.96, -129.85) * mm});
            skArc(sketch, "E293", {"start": v(119.4, -129.85) * mm, "mid": v(119.14, -129.92) * mm, "end": v(118.96, -130.1) * mm});
            skArc(sketch, "E294", {"start": v(118.28, -129.42) * mm, "mid": v(118.17, -130.2) * mm, "end": v(118.96, -130.1) * mm});
            skArc(sketch, "E295", {"start": v(118.28, -129.42) * mm, "mid": v(118.46, -129.24) * mm, "end": v(118.53, -128.99) * mm});
            skLineSegment(sketch, "E296", {"start": v(118.53, -124.52) * mm, "end": v(118.53, -128.99) * mm});
            skLineSegment(sketch, "E297", {"start": v(-119.4, 177.55) * mm, "end": v(-120.96, 177.55) * mm});
            skArc(sketch, "E298", {"start": v(-119.4, 177.55) * mm, "mid": v(-119.14, 177.61) * mm, "end": v(-118.96, 177.8) * mm});
            skArc(sketch, "E299", {"start": v(-118.28, 177.11) * mm, "mid": v(-118.17, 177.9) * mm, "end": v(-118.96, 177.8) * mm});
            skArc(sketch, "E300", {"start": v(-118.28, 177.11) * mm, "mid": v(-118.46, 176.93) * mm, "end": v(-118.53, 176.68) * mm});
            skLineSegment(sketch, "E301", {"start": v(-118.53, 172.21) * mm, "end": v(-118.53, 176.68) * mm});
            skArc(sketch, "E302", {"start": v(-118.53, 172.21) * mm, "mid": v(-118.46, 171.96) * mm, "end": v(-118.28, 171.78) * mm});
            skArc(sketch, "E303", {"start": v(-118.96, 171.1) * mm, "mid": v(-118.17, 171) * mm, "end": v(-118.28, 171.78) * mm});
            skArc(sketch, "E304", {"start": v(-118.96, 171.1) * mm, "mid": v(-119.14, 171.28) * mm, "end": v(-119.4, 171.35) * mm});
            skLineSegment(sketch, "E305", {"start": v(-120.96, 171.35) * mm, "end": v(-119.4, 171.35) * mm});
            skArc(sketch, "E306", {"start": v(-120.96, 171.35) * mm, "mid": v(-121.2, 171.28) * mm, "end": v(-121.4, 171.1) * mm});
            skArc(sketch, "E307", {"start": v(-122.07, 171.78) * mm, "mid": v(-122.18, 171) * mm, "end": v(-121.4, 171.1) * mm});
            skArc(sketch, "E308", {"start": v(-122.07, 171.78) * mm, "mid": v(-121.9, 171.96) * mm, "end": v(-121.82, 172.21) * mm});
            skLineSegment(sketch, "E309", {"start": v(-121.82, 176.68) * mm, "end": v(-121.82, 172.21) * mm});
            skArc(sketch, "E310", {"start": v(-121.82, 176.68) * mm, "mid": v(-121.9, 176.93) * mm, "end": v(-122.07, 177.11) * mm});
            skArc(sketch, "E311", {"start": v(-121.4, 177.8) * mm, "mid": v(-122.18, 177.9) * mm, "end": v(-122.07, 177.11) * mm});
            skArc(sketch, "E312", {"start": v(-121.4, 177.8) * mm, "mid": v(-121.2, 177.61) * mm, "end": v(-120.96, 177.55) * mm});
            skLineSegment(sketch, "E313", {"start": v(-119.4, 156.35) * mm, "end": v(-120.96, 156.35) * mm});
            skArc(sketch, "E314", {"start": v(-119.4, 156.35) * mm, "mid": v(-119.14, 156.41) * mm, "end": v(-118.96, 156.6) * mm});
            skArc(sketch, "E315", {"start": v(-118.28, 155.91) * mm, "mid": v(-118.17, 156.7) * mm, "end": v(-118.96, 156.6) * mm});
            skArc(sketch, "E316", {"start": v(-118.28, 155.91) * mm, "mid": v(-118.46, 155.73) * mm, "end": v(-118.53, 155.48) * mm});
            skLineSegment(sketch, "E317", {"start": v(-118.53, 151.01) * mm, "end": v(-118.53, 155.48) * mm});
            skArc(sketch, "E318", {"start": v(-118.53, 151.01) * mm, "mid": v(-118.46, 150.76) * mm, "end": v(-118.28, 150.58) * mm});
            skArc(sketch, "E319", {"start": v(-118.96, 149.9) * mm, "mid": v(-118.17, 149.8) * mm, "end": v(-118.28, 150.58) * mm});
            skArc(sketch, "E320", {"start": v(-118.96, 149.9) * mm, "mid": v(-119.14, 150.08) * mm, "end": v(-119.4, 150.15) * mm});
            skLineSegment(sketch, "E321", {"start": v(-120.96, 150.15) * mm, "end": v(-119.4, 150.15) * mm});
            skArc(sketch, "E322", {"start": v(-120.96, 150.15) * mm, "mid": v(-121.2, 150.08) * mm, "end": v(-121.4, 149.9) * mm});
            skArc(sketch, "E323", {"start": v(-122.07, 150.58) * mm, "mid": v(-122.18, 149.8) * mm, "end": v(-121.4, 149.9) * mm});
            skArc(sketch, "E324", {"start": v(-122.07, 150.58) * mm, "mid": v(-121.9, 150.76) * mm, "end": v(-121.82, 151.01) * mm});
            skLineSegment(sketch, "E325", {"start": v(-121.82, 155.48) * mm, "end": v(-121.82, 151.01) * mm});
            skArc(sketch, "E326", {"start": v(-121.82, 155.48) * mm, "mid": v(-121.9, 155.73) * mm, "end": v(-122.07, 155.91) * mm});
            skArc(sketch, "E327", {"start": v(-121.4, 156.6) * mm, "mid": v(-122.18, 156.7) * mm, "end": v(-122.07, 155.91) * mm});
            skArc(sketch, "E328", {"start": v(-121.4, 156.6) * mm, "mid": v(-121.2, 156.41) * mm, "end": v(-120.96, 156.35) * mm});
            skLineSegment(sketch, "E329", {"start": v(-119.4, 17.55) * mm, "end": v(-120.96, 17.55) * mm});
            skArc(sketch, "E330", {"start": v(-119.4, 17.55) * mm, "mid": v(-119.14, 17.61) * mm, "end": v(-118.96, 17.8) * mm});
            skArc(sketch, "E331", {"start": v(-118.28, 17.11) * mm, "mid": v(-118.17, 17.9) * mm, "end": v(-118.96, 17.8) * mm});
            skArc(sketch, "E332", {"start": v(-118.28, 17.11) * mm, "mid": v(-118.46, 16.93) * mm, "end": v(-118.53, 16.68) * mm});
            skLineSegment(sketch, "E333", {"start": v(-118.53, 12.21) * mm, "end": v(-118.53, 16.68) * mm});
            skArc(sketch, "E334", {"start": v(-118.53, 12.21) * mm, "mid": v(-118.46, 11.96) * mm, "end": v(-118.28, 11.78) * mm});
            skArc(sketch, "E335", {"start": v(-118.96, 11.1) * mm, "mid": v(-118.17, 11) * mm, "end": v(-118.28, 11.78) * mm});
            skArc(sketch, "E336", {"start": v(-118.96, 11.1) * mm, "mid": v(-119.14, 11.28) * mm, "end": v(-119.4, 11.35) * mm});
            skLineSegment(sketch, "E337", {"start": v(-120.96, 11.35) * mm, "end": v(-119.4, 11.35) * mm});
            skArc(sketch, "E338", {"start": v(-120.96, 11.35) * mm, "mid": v(-121.2, 11.28) * mm, "end": v(-121.4, 11.1) * mm});
            skArc(sketch, "E339", {"start": v(-122.07, 11.78) * mm, "mid": v(-122.18, 11) * mm, "end": v(-121.4, 11.1) * mm});
            skArc(sketch, "E340", {"start": v(-122.07, 11.78) * mm, "mid": v(-121.9, 11.96) * mm, "end": v(-121.82, 12.21) * mm});
            skLineSegment(sketch, "E341", {"start": v(-121.82, 16.68) * mm, "end": v(-121.82, 12.21) * mm});
            skArc(sketch, "E342", {"start": v(-121.82, 16.68) * mm, "mid": v(-121.9, 16.93) * mm, "end": v(-122.07, 17.11) * mm});
            skArc(sketch, "E343", {"start": v(-121.4, 17.8) * mm, "mid": v(-122.18, 17.9) * mm, "end": v(-122.07, 17.11) * mm});
            skArc(sketch, "E344", {"start": v(-121.4, 17.8) * mm, "mid": v(-121.2, 17.61) * mm, "end": v(-120.96, 17.55) * mm});
            skLineSegment(sketch, "E345", {"start": v(-119.4, -3.65) * mm, "end": v(-120.96, -3.65) * mm});
            skArc(sketch, "E346", {"start": v(-119.4, -3.65) * mm, "mid": v(-119.14, -3.59) * mm, "end": v(-118.96, -3.4) * mm});
            skArc(sketch, "E347", {"start": v(-118.28, -4.09) * mm, "mid": v(-118.17, -3.3) * mm, "end": v(-118.96, -3.4) * mm});
            skArc(sketch, "E348", {"start": v(-118.28, -4.09) * mm, "mid": v(-118.46, -4.27) * mm, "end": v(-118.53, -4.52) * mm});
            skLineSegment(sketch, "E349", {"start": v(-118.53, -8.99) * mm, "end": v(-118.53, -4.52) * mm});
            skArc(sketch, "E350", {"start": v(-118.53, -8.99) * mm, "mid": v(-118.46, -9.24) * mm, "end": v(-118.28, -9.42) * mm});
            skArc(sketch, "E351", {"start": v(-118.96, -10.1) * mm, "mid": v(-118.17, -10.2) * mm, "end": v(-118.28, -9.42) * mm});
            skArc(sketch, "E352", {"start": v(-118.96, -10.1) * mm, "mid": v(-119.14, -9.92) * mm, "end": v(-119.4, -9.85) * mm});
            skLineSegment(sketch, "E353", {"start": v(-120.96, -9.85) * mm, "end": v(-119.4, -9.85) * mm});
            skArc(sketch, "E354", {"start": v(-120.96, -9.85) * mm, "mid": v(-121.2, -9.92) * mm, "end": v(-121.4, -10.1) * mm});
            skArc(sketch, "E355", {"start": v(-122.07, -9.42) * mm, "mid": v(-122.18, -10.2) * mm, "end": v(-121.4, -10.1) * mm});
            skArc(sketch, "E356", {"start": v(-122.07, -9.42) * mm, "mid": v(-121.9, -9.24) * mm, "end": v(-121.82, -8.99) * mm});
            skLineSegment(sketch, "E357", {"start": v(-121.82, -4.52) * mm, "end": v(-121.82, -8.99) * mm});
            skArc(sketch, "E358", {"start": v(-121.82, -4.52) * mm, "mid": v(-121.9, -4.27) * mm, "end": v(-122.07, -4.09) * mm});
            skArc(sketch, "E359", {"start": v(-121.4, -3.4) * mm, "mid": v(-122.18, -3.3) * mm, "end": v(-122.07, -4.09) * mm});
            skArc(sketch, "E360", {"start": v(-121.4, -3.4) * mm, "mid": v(-121.2, -3.59) * mm, "end": v(-120.96, -3.65) * mm});
            skArc(sketch, "E361", {"start": v(-121.82, -103.32) * mm, "mid": v(-121.9, -103.07) * mm, "end": v(-122.07, -102.89) * mm});
            skArc(sketch, "E362", {"start": v(-121.4, -102.2) * mm, "mid": v(-122.18, -102.1) * mm, "end": v(-122.07, -102.89) * mm});
            skArc(sketch, "E363", {"start": v(-121.4, -102.2) * mm, "mid": v(-121.2, -102.39) * mm, "end": v(-120.96, -102.45) * mm});
            skLineSegment(sketch, "E364", {"start": v(-119.4, -102.45) * mm, "end": v(-120.96, -102.45) * mm});
            skArc(sketch, "E365", {"start": v(-119.4, -102.45) * mm, "mid": v(-119.14, -102.39) * mm, "end": v(-118.96, -102.2) * mm});
            skArc(sketch, "E366", {"start": v(-118.28, -102.89) * mm, "mid": v(-118.17, -102.1) * mm, "end": v(-118.96, -102.2) * mm});
            skArc(sketch, "E367", {"start": v(-118.28, -102.89) * mm, "mid": v(-118.46, -103.07) * mm, "end": v(-118.53, -103.32) * mm});
            skLineSegment(sketch, "E368", {"start": v(-118.52, -107.79) * mm, "end": v(-118.53, -103.32) * mm});
            skArc(sketch, "E369", {"start": v(-118.52, -107.79) * mm, "mid": v(-118.46, -108.04) * mm, "end": v(-118.27, -108.22) * mm});
            skArc(sketch, "E370", {"start": v(-118.96, -108.9) * mm, "mid": v(-118.17, -109) * mm, "end": v(-118.27, -108.22) * mm});
            skArc(sketch, "E371", {"start": v(-118.96, -108.9) * mm, "mid": v(-119.14, -108.72) * mm, "end": v(-119.4, -108.65) * mm});
            skLineSegment(sketch, "E372", {"start": v(-120.96, -108.65) * mm, "end": v(-119.4, -108.65) * mm});
            skArc(sketch, "E373", {"start": v(-120.96, -108.65) * mm, "mid": v(-121.2, -108.72) * mm, "end": v(-121.4, -108.9) * mm});
            skArc(sketch, "E374", {"start": v(-122.07, -108.22) * mm, "mid": v(-122.18, -109) * mm, "end": v(-121.4, -108.9) * mm});
            skArc(sketch, "E375", {"start": v(-122.07, -108.22) * mm, "mid": v(-121.9, -108.04) * mm, "end": v(-121.82, -107.79) * mm});
            skLineSegment(sketch, "E376", {"start": v(-121.82, -103.32) * mm, "end": v(-121.82, -107.79) * mm});
            skArc(sketch, "E377", {"start": v(-121.82, -124.52) * mm, "mid": v(-121.9, -124.27) * mm, "end": v(-122.07, -124.09) * mm});
            skArc(sketch, "E378", {"start": v(-121.4, -123.4) * mm, "mid": v(-122.18, -123.3) * mm, "end": v(-122.07, -124.09) * mm});
            skArc(sketch, "E379", {"start": v(-121.4, -123.4) * mm, "mid": v(-121.2, -123.59) * mm, "end": v(-120.96, -123.65) * mm});
            skLineSegment(sketch, "E380", {"start": v(-119.4, -123.65) * mm, "end": v(-120.96, -123.65) * mm});
            skArc(sketch, "E381", {"start": v(-119.4, -123.65) * mm, "mid": v(-119.14, -123.59) * mm, "end": v(-118.96, -123.4) * mm});
            skArc(sketch, "E382", {"start": v(-118.28, -124.09) * mm, "mid": v(-118.17, -123.3) * mm, "end": v(-118.96, -123.4) * mm});
            skArc(sketch, "E383", {"start": v(-118.28, -124.09) * mm, "mid": v(-118.46, -124.27) * mm, "end": v(-118.52, -124.52) * mm});
            skLineSegment(sketch, "E384", {"start": v(-118.52, -128.99) * mm, "end": v(-118.53, -124.52) * mm});
            skArc(sketch, "E385", {"start": v(-118.52, -128.99) * mm, "mid": v(-118.46, -129.24) * mm, "end": v(-118.27, -129.42) * mm});
            skArc(sketch, "E386", {"start": v(-118.96, -130.1) * mm, "mid": v(-118.17, -130.2) * mm, "end": v(-118.27, -129.42) * mm});
            skArc(sketch, "E387", {"start": v(-118.96, -130.1) * mm, "mid": v(-119.14, -129.92) * mm, "end": v(-119.4, -129.85) * mm});
            skLineSegment(sketch, "E388", {"start": v(-120.96, -129.85) * mm, "end": v(-119.4, -129.85) * mm});
            skArc(sketch, "E389", {"start": v(-120.96, -129.85) * mm, "mid": v(-121.2, -129.92) * mm, "end": v(-121.4, -130.1) * mm});
            skArc(sketch, "E390", {"start": v(-122.07, -129.42) * mm, "mid": v(-122.18, -130.2) * mm, "end": v(-121.4, -130.1) * mm});
            skArc(sketch, "E391", {"start": v(-122.07, -129.42) * mm, "mid": v(-121.9, -129.24) * mm, "end": v(-121.82, -128.99) * mm});
            skLineSegment(sketch, "E392", {"start": v(-121.82, -124.52) * mm, "end": v(-121.82, -128.99) * mm});
            skLineSegment(sketch, "E393", {"start": v(-140, -142.45) * mm, "end": v(-141.56, -142.45) * mm});
            skArc(sketch, "E394", {"start": v(-140, -142.45) * mm, "mid": v(-139.75, -142.39) * mm, "end": v(-139.56, -142.2) * mm});
            skArc(sketch, "E395", {"start": v(-138.88, -142.89) * mm, "mid": v(-138.78, -142.1) * mm, "end": v(-139.56, -142.2) * mm});
            skArc(sketch, "E396", {"start": v(-138.88, -142.89) * mm, "mid": v(-139.06, -143.07) * mm, "end": v(-139.13, -143.32) * mm});
            skLineSegment(sketch, "E397", {"start": v(-139.13, -147.79) * mm, "end": v(-139.13, -143.32) * mm});
            skArc(sketch, "E398", {"start": v(-139.13, -147.79) * mm, "mid": v(-139.06, -148.04) * mm, "end": v(-138.88, -148.22) * mm});
            skArc(sketch, "E399", {"start": v(-139.56, -148.9) * mm, "mid": v(-138.78, -149) * mm, "end": v(-138.88, -148.22) * mm});
            skArc(sketch, "E400", {"start": v(-139.56, -148.9) * mm, "mid": v(-139.75, -148.72) * mm, "end": v(-140, -148.65) * mm});
            skLineSegment(sketch, "E401", {"start": v(-141.56, -148.65) * mm, "end": v(-140, -148.65) * mm});
            skArc(sketch, "E402", {"start": v(-141.56, -148.65) * mm, "mid": v(-141.81, -148.72) * mm, "end": v(-142, -148.9) * mm});
            skArc(sketch, "E403", {"start": v(-142.68, -148.22) * mm, "mid": v(-142.78, -149) * mm, "end": v(-142, -148.9) * mm});
            skArc(sketch, "E404", {"start": v(-142.68, -148.22) * mm, "mid": v(-142.5, -148.04) * mm, "end": v(-142.43, -147.79) * mm});
            skLineSegment(sketch, "E405", {"start": v(-142.43, -143.32) * mm, "end": v(-142.43, -147.79) * mm});
            skArc(sketch, "E406", {"start": v(-142.43, -143.32) * mm, "mid": v(-142.5, -143.07) * mm, "end": v(-142.68, -142.89) * mm});
            skArc(sketch, "E407", {"start": v(-142, -142.2) * mm, "mid": v(-142.78, -142.1) * mm, "end": v(-142.68, -142.89) * mm});
            skArc(sketch, "E408", {"start": v(-142, -142.2) * mm, "mid": v(-141.81, -142.39) * mm, "end": v(-141.56, -142.45) * mm});
            skLineSegment(sketch, "E409", {"start": v(-140, -163.65) * mm, "end": v(-141.56, -163.65) * mm});
            skArc(sketch, "E410", {"start": v(-140, -163.65) * mm, "mid": v(-139.75, -163.59) * mm, "end": v(-139.56, -163.4) * mm});
            skArc(sketch, "E411", {"start": v(-138.88, -164.09) * mm, "mid": v(-138.78, -163.3) * mm, "end": v(-139.56, -163.4) * mm});
            skArc(sketch, "E412", {"start": v(-138.88, -164.09) * mm, "mid": v(-139.06, -164.27) * mm, "end": v(-139.13, -164.52) * mm});
            skLineSegment(sketch, "E413", {"start": v(-139.13, -168.99) * mm, "end": v(-139.13, -164.52) * mm});
            skArc(sketch, "E414", {"start": v(-139.13, -168.99) * mm, "mid": v(-139.06, -169.24) * mm, "end": v(-138.88, -169.42) * mm});
            skArc(sketch, "E415", {"start": v(-139.56, -170.1) * mm, "mid": v(-138.78, -170.2) * mm, "end": v(-138.88, -169.42) * mm});
            skArc(sketch, "E416", {"start": v(-139.56, -170.1) * mm, "mid": v(-139.75, -169.92) * mm, "end": v(-140, -169.85) * mm});
            skLineSegment(sketch, "E417", {"start": v(-141.56, -169.85) * mm, "end": v(-140, -169.85) * mm});
            skArc(sketch, "E418", {"start": v(-141.56, -169.85) * mm, "mid": v(-141.81, -169.92) * mm, "end": v(-142, -170.1) * mm});
            skArc(sketch, "E419", {"start": v(-142.68, -169.42) * mm, "mid": v(-142.78, -170.2) * mm, "end": v(-142, -170.1) * mm});
            skArc(sketch, "E420", {"start": v(-142.68, -169.42) * mm, "mid": v(-142.5, -169.24) * mm, "end": v(-142.43, -168.99) * mm});
            skLineSegment(sketch, "E421", {"start": v(-142.43, -164.52) * mm, "end": v(-142.43, -168.99) * mm});
            skArc(sketch, "E422", {"start": v(-142.43, -164.52) * mm, "mid": v(-142.5, -164.27) * mm, "end": v(-142.68, -164.09) * mm});
            skArc(sketch, "E423", {"start": v(-142, -163.4) * mm, "mid": v(-142.78, -163.3) * mm, "end": v(-142.68, -164.09) * mm});
            skArc(sketch, "E424", {"start": v(-142, -163.4) * mm, "mid": v(-141.81, -163.59) * mm, "end": v(-141.56, -163.65) * mm});
            skLineSegment(sketch, "E425", {"start": v(-157.8, -128.72) * mm, "end": v(-157.8, -130.3) * mm});
            skArc(sketch, "E426", {"start": v(-157.8, -128.72) * mm, "mid": v(-157.87, -128.47) * mm, "end": v(-158.05, -128.3) * mm});
            skArc(sketch, "E427", {"start": v(-157.37, -127.6) * mm, "mid": v(-158.15, -127.5) * mm, "end": v(-158.05, -128.3) * mm});
            skArc(sketch, "E428", {"start": v(-157.37, -127.6) * mm, "mid": v(-157.18, -127.8) * mm, "end": v(-156.93, -127.86) * mm});
            skLineSegment(sketch, "E429", {"start": v(-152.47, -127.86) * mm, "end": v(-156.93, -127.86) * mm});
            skArc(sketch, "E430", {"start": v(-152.47, -127.86) * mm, "mid": v(-152.22, -127.8) * mm, "end": v(-152.03, -127.6) * mm});
            skArc(sketch, "E431", {"start": v(-151.35, -128.3) * mm, "mid": v(-151.25, -127.5) * mm, "end": v(-152.03, -127.6) * mm});
            skArc(sketch, "E432", {"start": v(-151.35, -128.3) * mm, "mid": v(-151.53, -128.47) * mm, "end": v(-151.6, -128.72) * mm});
            skLineSegment(sketch, "E433", {"start": v(-151.6, -130.3) * mm, "end": v(-151.6, -128.72) * mm});
            skArc(sketch, "E434", {"start": v(-151.6, -130.3) * mm, "mid": v(-151.53, -130.54) * mm, "end": v(-151.35, -130.72) * mm});
            skArc(sketch, "E435", {"start": v(-152.03, -131.4) * mm, "mid": v(-151.25, -131.51) * mm, "end": v(-151.35, -130.72) * mm});
            skArc(sketch, "E436", {"start": v(-152.03, -131.4) * mm, "mid": v(-152.22, -131.22) * mm, "end": v(-152.47, -131.16) * mm});
            skLineSegment(sketch, "E437", {"start": v(-156.93, -131.16) * mm, "end": v(-152.47, -131.16) * mm});
            skArc(sketch, "E438", {"start": v(-156.93, -131.16) * mm, "mid": v(-157.18, -131.22) * mm, "end": v(-157.37, -131.4) * mm});
            skArc(sketch, "E439", {"start": v(-158.05, -130.72) * mm, "mid": v(-158.15, -131.51) * mm, "end": v(-157.37, -131.4) * mm});
            skArc(sketch, "E440", {"start": v(-158.05, -130.72) * mm, "mid": v(-157.87, -130.54) * mm, "end": v(-157.8, -130.3) * mm});
            skLineSegment(sketch, "E441", {"start": v(-179, -128.72) * mm, "end": v(-179, -130.3) * mm});
            skArc(sketch, "E442", {"start": v(-179, -128.72) * mm, "mid": v(-179.07, -128.47) * mm, "end": v(-179.25, -128.3) * mm});
            skArc(sketch, "E443", {"start": v(-178.57, -127.6) * mm, "mid": v(-179.35, -127.5) * mm, "end": v(-179.25, -128.3) * mm});
            skArc(sketch, "E444", {"start": v(-178.57, -127.6) * mm, "mid": v(-178.38, -127.8) * mm, "end": v(-178.13, -127.86) * mm});
            skLineSegment(sketch, "E445", {"start": v(-173.67, -127.86) * mm, "end": v(-178.13, -127.86) * mm});
            skArc(sketch, "E446", {"start": v(-173.67, -127.86) * mm, "mid": v(-173.42, -127.8) * mm, "end": v(-173.23, -127.6) * mm});
            skArc(sketch, "E447", {"start": v(-172.55, -128.3) * mm, "mid": v(-172.45, -127.5) * mm, "end": v(-173.23, -127.6) * mm});
            skArc(sketch, "E448", {"start": v(-172.55, -128.3) * mm, "mid": v(-172.73, -128.47) * mm, "end": v(-172.8, -128.72) * mm});
            skLineSegment(sketch, "E449", {"start": v(-172.8, -130.3) * mm, "end": v(-172.8, -128.72) * mm});
            skArc(sketch, "E450", {"start": v(-172.8, -130.3) * mm, "mid": v(-172.73, -130.54) * mm, "end": v(-172.55, -130.72) * mm});
            skArc(sketch, "E451", {"start": v(-173.23, -131.4) * mm, "mid": v(-172.45, -131.51) * mm, "end": v(-172.55, -130.72) * mm});
            skArc(sketch, "E452", {"start": v(-173.23, -131.4) * mm, "mid": v(-173.42, -131.22) * mm, "end": v(-173.67, -131.16) * mm});
            skLineSegment(sketch, "E453", {"start": v(-178.13, -131.16) * mm, "end": v(-173.67, -131.16) * mm});
            skArc(sketch, "E454", {"start": v(-178.13, -131.16) * mm, "mid": v(-178.38, -131.22) * mm, "end": v(-178.57, -131.4) * mm});
            skArc(sketch, "E455", {"start": v(-179.25, -130.72) * mm, "mid": v(-179.35, -131.51) * mm, "end": v(-178.57, -131.4) * mm});
            skArc(sketch, "E456", {"start": v(-179.25, -130.72) * mm, "mid": v(-179.07, -130.54) * mm, "end": v(-179, -130.3) * mm});
            skLineSegment(sketch, "E457", {"start": v(-189.04, -142.45) * mm, "end": v(-190.6, -142.45) * mm});
            skArc(sketch, "E458", {"start": v(-189.04, -142.45) * mm, "mid": v(-188.79, -142.39) * mm, "end": v(-188.6, -142.2) * mm});
            skArc(sketch, "E459", {"start": v(-187.92, -142.89) * mm, "mid": v(-187.82, -142.1) * mm, "end": v(-188.6, -142.2) * mm});
            skArc(sketch, "E460", {"start": v(-187.92, -142.89) * mm, "mid": v(-188.1, -143.07) * mm, "end": v(-188.17, -143.32) * mm});
            skLineSegment(sketch, "E461", {"start": v(-188.17, -147.79) * mm, "end": v(-188.17, -143.32) * mm});
            skArc(sketch, "E462", {"start": v(-188.17, -147.79) * mm, "mid": v(-188.1, -148.04) * mm, "end": v(-187.92, -148.22) * mm});
            skArc(sketch, "E463", {"start": v(-188.6, -148.9) * mm, "mid": v(-187.82, -149) * mm, "end": v(-187.92, -148.22) * mm});
            skArc(sketch, "E464", {"start": v(-188.6, -148.9) * mm, "mid": v(-188.79, -148.72) * mm, "end": v(-189.04, -148.65) * mm});
            skLineSegment(sketch, "E465", {"start": v(-190.6, -148.65) * mm, "end": v(-189.04, -148.65) * mm});
            skArc(sketch, "E466", {"start": v(-190.6, -148.65) * mm, "mid": v(-190.85, -148.72) * mm, "end": v(-191.04, -148.9) * mm});
            skArc(sketch, "E467", {"start": v(-191.72, -148.22) * mm, "mid": v(-191.82, -149) * mm, "end": v(-191.04, -148.9) * mm});
            skArc(sketch, "E468", {"start": v(-191.72, -148.22) * mm, "mid": v(-191.54, -148.04) * mm, "end": v(-191.47, -147.79) * mm});
            skLineSegment(sketch, "E469", {"start": v(-191.47, -143.32) * mm, "end": v(-191.47, -147.79) * mm});
            skArc(sketch, "E470", {"start": v(-191.47, -143.32) * mm, "mid": v(-191.54, -143.07) * mm, "end": v(-191.72, -142.89) * mm});
            skArc(sketch, "E471", {"start": v(-191.04, -142.2) * mm, "mid": v(-191.82, -142.1) * mm, "end": v(-191.72, -142.89) * mm});
            skArc(sketch, "E472", {"start": v(-191.04, -142.2) * mm, "mid": v(-190.85, -142.39) * mm, "end": v(-190.6, -142.45) * mm});
            skLineSegment(sketch, "E473", {"start": v(-189.04, -163.65) * mm, "end": v(-190.6, -163.65) * mm});
            skArc(sketch, "E474", {"start": v(-189.04, -163.65) * mm, "mid": v(-188.79, -163.59) * mm, "end": v(-188.6, -163.4) * mm});
            skArc(sketch, "E475", {"start": v(-187.92, -164.09) * mm, "mid": v(-187.82, -163.3) * mm, "end": v(-188.6, -163.4) * mm});
            skArc(sketch, "E476", {"start": v(-187.92, -164.09) * mm, "mid": v(-188.1, -164.27) * mm, "end": v(-188.17, -164.52) * mm});
            skLineSegment(sketch, "E477", {"start": v(-188.17, -168.99) * mm, "end": v(-188.17, -164.52) * mm});
            skArc(sketch, "E478", {"start": v(-188.17, -168.99) * mm, "mid": v(-188.1, -169.24) * mm, "end": v(-187.92, -169.42) * mm});
            skArc(sketch, "E479", {"start": v(-188.6, -170.1) * mm, "mid": v(-187.82, -170.2) * mm, "end": v(-187.92, -169.42) * mm});
            skArc(sketch, "E480", {"start": v(-188.6, -170.1) * mm, "mid": v(-188.79, -169.92) * mm, "end": v(-189.04, -169.85) * mm});
            skLineSegment(sketch, "E481", {"start": v(-190.6, -169.85) * mm, "end": v(-189.04, -169.85) * mm});
            skArc(sketch, "E482", {"start": v(-190.6, -169.85) * mm, "mid": v(-190.85, -169.92) * mm, "end": v(-191.04, -170.1) * mm});
            skArc(sketch, "E483", {"start": v(-191.72, -169.42) * mm, "mid": v(-191.82, -170.2) * mm, "end": v(-191.04, -170.1) * mm});
            skArc(sketch, "E484", {"start": v(-191.72, -169.42) * mm, "mid": v(-191.54, -169.24) * mm, "end": v(-191.47, -168.99) * mm});
            skLineSegment(sketch, "E485", {"start": v(-191.47, -164.52) * mm, "end": v(-191.47, -168.99) * mm});
            skArc(sketch, "E486", {"start": v(-191.47, -164.52) * mm, "mid": v(-191.54, -164.27) * mm, "end": v(-191.72, -164.09) * mm});
            skArc(sketch, "E487", {"start": v(-191.04, -163.4) * mm, "mid": v(-191.82, -163.3) * mm, "end": v(-191.72, -164.09) * mm});
            skArc(sketch, "E488", {"start": v(-191.04, -163.4) * mm, "mid": v(-190.85, -163.59) * mm, "end": v(-190.6, -163.65) * mm});
            skLineSegment(sketch, "E489", {"start": v(120.96, -142.45) * mm, "end": v(119.4, -142.45) * mm});
            skArc(sketch, "E490", {"start": v(120.96, -142.45) * mm, "mid": v(121.2, -142.39) * mm, "end": v(121.4, -142.2) * mm});
            skArc(sketch, "E491", {"start": v(122.07, -142.89) * mm, "mid": v(122.18, -142.1) * mm, "end": v(121.4, -142.2) * mm});
            skArc(sketch, "E492", {"start": v(122.07, -142.89) * mm, "mid": v(121.9, -143.07) * mm, "end": v(121.82, -143.32) * mm});
            skLineSegment(sketch, "E493", {"start": v(121.82, -168.99) * mm, "end": v(121.82, -143.32) * mm});
            skArc(sketch, "E494", {"start": v(121.82, -168.99) * mm, "mid": v(121.9, -169.24) * mm, "end": v(122.07, -169.42) * mm});
            skArc(sketch, "E495", {"start": v(121.4, -170.1) * mm, "mid": v(122.18, -170.2) * mm, "end": v(122.07, -169.42) * mm});
            skArc(sketch, "E496", {"start": v(121.4, -170.1) * mm, "mid": v(121.2, -169.92) * mm, "end": v(120.96, -169.85) * mm});
            skLineSegment(sketch, "E497", {"start": v(119.4, -169.85) * mm, "end": v(120.96, -169.85) * mm});
            skArc(sketch, "E498", {"start": v(119.4, -169.85) * mm, "mid": v(119.14, -169.92) * mm, "end": v(118.96, -170.1) * mm});
            skArc(sketch, "E499", {"start": v(118.28, -169.42) * mm, "mid": v(118.17, -170.2) * mm, "end": v(118.96, -170.1) * mm});
            skArc(sketch, "E500", {"start": v(118.28, -169.42) * mm, "mid": v(118.46, -169.24) * mm, "end": v(118.53, -168.99) * mm});
            skLineSegment(sketch, "E501", {"start": v(118.53, -143.32) * mm, "end": v(118.53, -168.99) * mm});
            skArc(sketch, "E502", {"start": v(118.53, -143.32) * mm, "mid": v(118.46, -143.07) * mm, "end": v(118.28, -142.89) * mm});
            skArc(sketch, "E503", {"start": v(118.96, -142.2) * mm, "mid": v(118.17, -142.1) * mm, "end": v(118.28, -142.89) * mm});
            skArc(sketch, "E504", {"start": v(118.96, -142.2) * mm, "mid": v(119.14, -142.39) * mm, "end": v(119.4, -142.45) * mm});
            skLineSegment(sketch, "E505", {"start": v(-119.4, -142.45) * mm, "end": v(-120.96, -142.45) * mm});
            skArc(sketch, "E506", {"start": v(-119.4, -142.45) * mm, "mid": v(-119.14, -142.39) * mm, "end": v(-118.96, -142.2) * mm});
            skArc(sketch, "E507", {"start": v(-118.28, -142.89) * mm, "mid": v(-118.17, -142.1) * mm, "end": v(-118.96, -142.2) * mm});
            skArc(sketch, "E508", {"start": v(-118.28, -142.89) * mm, "mid": v(-118.46, -143.07) * mm, "end": v(-118.53, -143.32) * mm});
            skLineSegment(sketch, "E509", {"start": v(-118.53, -168.99) * mm, "end": v(-118.53, -143.32) * mm});
            skArc(sketch, "E510", {"start": v(-118.53, -168.99) * mm, "mid": v(-118.46, -169.24) * mm, "end": v(-118.28, -169.42) * mm});
            skArc(sketch, "E511", {"start": v(-118.96, -170.1) * mm, "mid": v(-118.17, -170.2) * mm, "end": v(-118.28, -169.42) * mm});
            skArc(sketch, "E512", {"start": v(-118.96, -170.1) * mm, "mid": v(-119.14, -169.92) * mm, "end": v(-119.4, -169.85) * mm});
            skLineSegment(sketch, "E513", {"start": v(-120.96, -169.85) * mm, "end": v(-119.4, -169.85) * mm});
            skArc(sketch, "E514", {"start": v(-120.96, -169.85) * mm, "mid": v(-121.2, -169.92) * mm, "end": v(-121.4, -170.1) * mm});
            skArc(sketch, "E515", {"start": v(-122.07, -169.42) * mm, "mid": v(-122.18, -170.2) * mm, "end": v(-121.4, -170.1) * mm});
            skArc(sketch, "E516", {"start": v(-122.07, -169.42) * mm, "mid": v(-121.9, -169.24) * mm, "end": v(-121.82, -168.99) * mm});
            skLineSegment(sketch, "E517", {"start": v(-121.82, -143.32) * mm, "end": v(-121.82, -168.99) * mm});
            skArc(sketch, "E518", {"start": v(-121.82, -143.32) * mm, "mid": v(-121.9, -143.07) * mm, "end": v(-122.07, -142.89) * mm});
            skArc(sketch, "E519", {"start": v(-121.4, -142.2) * mm, "mid": v(-122.18, -142.1) * mm, "end": v(-122.07, -142.89) * mm});
            skArc(sketch, "E520", {"start": v(-121.4, -142.2) * mm, "mid": v(-121.2, -142.39) * mm, "end": v(-120.96, -142.45) * mm});
            skLineSegment(sketch, "E521", {"start": v(107, 138.85) * mm, "end": v(-107, 138.85) * mm});
            skArc(sketch, "E522", {"start": v(115, 130.85) * mm, "mid": v(112.66, 136.5) * mm, "end": v(107, 138.85) * mm});
            skLineSegment(sketch, "E523", {"start": v(115, -136.05) * mm, "end": v(115, 130.85) * mm});
            skArc(sketch, "E524", {"start": v(107, -144.03) * mm, "mid": v(112.65, -141.7) * mm, "end": v(115, -136.05) * mm});
            skLineSegment(sketch, "E525", {"start": v(30.55, -144.03) * mm, "end": v(107, -144.03) * mm});
            skArc(sketch, "E526", {"start": v(30.55, -144.03) * mm, "mid": v(27.95, -144.76) * mm, "end": v(26.1, -146.73) * mm});
            skLineSegment(sketch, "E527", {"start": v(17.44, -163.45) * mm, "end": v(26.1, -146.73) * mm});
            skArc(sketch, "E528", {"start": v(13, -166.15) * mm, "mid": v(15.6, -165.42) * mm, "end": v(17.44, -163.45) * mm});
            skLineSegment(sketch, "E529", {"start": v(-13, -166.15) * mm, "end": v(13, -166.15) * mm});
            skArc(sketch, "E530", {"start": v(-17.45, -163.44) * mm, "mid": v(-15.6, -165.42) * mm, "end": v(-13, -166.15) * mm});
            skLineSegment(sketch, "E531", {"start": v(-26.03, -146.74) * mm, "end": v(-17.45, -163.44) * mm});
            skArc(sketch, "E532", {"start": v(-26.03, -146.74) * mm, "mid": v(-27.87, -144.76) * mm, "end": v(-30.48, -144.03) * mm});
            skLineSegment(sketch, "E533", {"start": v(-107, -144.03) * mm, "end": v(-30.48, -144.03) * mm});
            skArc(sketch, "E534", {"start": v(-115, -136.05) * mm, "mid": v(-112.65, -141.7) * mm, "end": v(-107, -144.03) * mm});
            skLineSegment(sketch, "E535", {"start": v(-115, 130.85) * mm, "end": v(-115, -136.05) * mm});
            skArc(sketch, "E536", {"start": v(-107, 138.85) * mm, "mid": v(-112.66, 136.5) * mm, "end": v(-115, 130.85) * mm});
            skArc(sketch, "E537", {"start": v(190, -181.15) * mm, "mid": v(193.54, -179.69) * mm, "end": v(195, -176.15) * mm});
            skLineSegment(sketch, "E538", {"start": v(195, -176.15) * mm, "end": v(195, -127.62) * mm});
            skArc(sketch, "E539", {"start": v(195, -127.62) * mm, "mid": v(194.55, -125.34) * mm, "end": v(193.27, -123.4) * mm});
            skLineSegment(sketch, "E540", {"start": v(193.27, -123.4) * mm, "end": v(188.73, -118.8) * mm});
            skArc(sketch, "E541", {"start": v(187, -114.6) * mm, "mid": v(187.45, -116.87) * mm, "end": v(188.73, -118.8) * mm});
            skLineSegment(sketch, "E542", {"start": v(187, -114.6) * mm, "end": v(187, 166.36) * mm});
            skArc(sketch, "E543", {"start": v(188.76, 170.6) * mm, "mid": v(187.46, 168.66) * mm, "end": v(187, 166.36) * mm});
            skLineSegment(sketch, "E544", {"start": v(188.76, 170.6) * mm, "end": v(193.24, 175.09) * mm});
            skArc(sketch, "E545", {"start": v(193.24, 175.09) * mm, "mid": v(194.54, 177.04) * mm, "end": v(195, 179.33) * mm});
            skLineSegment(sketch, "E546", {"start": v(195, 179.33) * mm, "end": v(195, 188.85) * mm});
            skLineSegment(sketch, "E547", {"start": v(195, 188.85) * mm, "end": v(185, 188.85) * mm});
            skLineSegment(sketch, "E548", {"start": v(185, 188.85) * mm, "end": v(185, 186.61) * mm});
            skArc(sketch, "E549", {"start": v(185, 186.61) * mm, "mid": v(185.07, 186.36) * mm, "end": v(185.25, 186.18) * mm});
            skArc(sketch, "E550", {"start": v(184.57, 185.5) * mm, "mid": v(185.35, 185.4) * mm, "end": v(185.25, 186.18) * mm});
            skArc(sketch, "E551", {"start": v(184.57, 185.5) * mm, "mid": v(184.38, 185.68) * mm, "end": v(184.13, 185.75) * mm});
            skLineSegment(sketch, "E552", {"start": v(184.13, 185.75) * mm, "end": v(160.78, 185.75) * mm});
            skLineSegment(sketch, "E553", {"start": v(160.78, 185.75) * mm, "end": v(160.78, 182.75) * mm});
            skLineSegment(sketch, "E554", {"start": v(160.78, 182.75) * mm, "end": v(162.05, 182.75) * mm});
            skLineSegment(sketch, "E555", {"start": v(162.05, 182.75) * mm, "end": v(162.05, 178.75) * mm});
            skLineSegment(sketch, "E556", {"start": v(162.05, 178.75) * mm, "end": v(160.78, 178.75) * mm});
            skLineSegment(sketch, "E557", {"start": v(160.78, 178.75) * mm, "end": v(160.78, 175.75) * mm});
            skLineSegment(sketch, "E558", {"start": v(160.78, 175.75) * mm, "end": v(157.57, 175.75) * mm});
            skLineSegment(sketch, "E559", {"start": v(157.57, 175.75) * mm, "end": v(157.57, 178.75) * mm});
            skLineSegment(sketch, "E560", {"start": v(157.57, 178.75) * mm, "end": v(156.3, 178.75) * mm});
            skLineSegment(sketch, "E561", {"start": v(156.3, 178.75) * mm, "end": v(156.3, 182.75) * mm});
            skLineSegment(sketch, "E562", {"start": v(156.3, 182.75) * mm, "end": v(157.57, 182.75) * mm});
            skLineSegment(sketch, "E563", {"start": v(157.57, 182.75) * mm, "end": v(157.57, 185.75) * mm});
            skLineSegment(sketch, "E564", {"start": v(157.57, 185.75) * mm, "end": v(134.07, 185.75) * mm});
            skArc(sketch, "E565", {"start": v(134.07, 185.75) * mm, "mid": v(133.82, 185.68) * mm, "end": v(133.63, 185.5) * mm});
            skArc(sketch, "E566", {"start": v(132.95, 186.18) * mm, "mid": v(132.85, 185.4) * mm, "end": v(133.63, 185.5) * mm});
            skArc(sketch, "E567", {"start": v(132.95, 186.18) * mm, "mid": v(133.13, 186.36) * mm, "end": v(133.2, 186.61) * mm});
            skLineSegment(sketch, "E568", {"start": v(133.2, 186.61) * mm, "end": v(133.2, 188.85) * mm});
            skLineSegment(sketch, "E569", {"start": v(133.2, 188.85) * mm, "end": v(51.73, 188.85) * mm});
            skLineSegment(sketch, "E570", {"start": v(51.73, 188.85) * mm, "end": v(51.73, 186.61) * mm});
            skArc(sketch, "E571", {"start": v(51.73, 186.61) * mm, "mid": v(51.8, 186.36) * mm, "end": v(51.98, 186.18) * mm});
            skArc(sketch, "E572", {"start": v(51.3, 185.5) * mm, "mid": v(52.09, 185.4) * mm, "end": v(51.98, 186.18) * mm});
            skArc(sketch, "E573", {"start": v(51.3, 185.5) * mm, "mid": v(51.12, 185.68) * mm, "end": v(50.87, 185.75) * mm});
            skLineSegment(sketch, "E574", {"start": v(50.87, 185.75) * mm, "end": v(44.1, 185.75) * mm});
            skLineSegment(sketch, "E575", {"start": v(44.1, 185.75) * mm, "end": v(44.1, 182.75) * mm});
            skLineSegment(sketch, "E576", {"start": v(44.1, 182.75) * mm, "end": v(45.38, 182.75) * mm});
            skLineSegment(sketch, "E577", {"start": v(45.38, 182.75) * mm, "end": v(45.38, 178.75) * mm});
            skLineSegment(sketch, "E578", {"start": v(45.38, 178.75) * mm, "end": v(44.1, 178.75) * mm});
            skLineSegment(sketch, "E579", {"start": v(44.1, 178.75) * mm, "end": v(44.1, 175.75) * mm});
            skLineSegment(sketch, "E580", {"start": v(44.1, 175.75) * mm, "end": v(40.9, 175.75) * mm});
            skLineSegment(sketch, "E581", {"start": v(40.9, 175.75) * mm, "end": v(40.9, 178.75) * mm});
            skLineSegment(sketch, "E582", {"start": v(40.9, 178.75) * mm, "end": v(39.63, 178.75) * mm});
            skLineSegment(sketch, "E583", {"start": v(39.63, 178.75) * mm, "end": v(39.63, 182.75) * mm});
            skLineSegment(sketch, "E584", {"start": v(39.63, 182.75) * mm, "end": v(40.9, 182.75) * mm});
            skLineSegment(sketch, "E585", {"start": v(40.9, 182.75) * mm, "end": v(40.9, 185.75) * mm});
            skLineSegment(sketch, "E586", {"start": v(40.9, 185.75) * mm, "end": v(34.13, 185.75) * mm});
            skArc(sketch, "E587", {"start": v(34.13, 185.75) * mm, "mid": v(33.88, 185.68) * mm, "end": v(33.7, 185.5) * mm});
            skArc(sketch, "E588", {"start": v(33.02, 186.18) * mm, "mid": v(32.91, 185.4) * mm, "end": v(33.7, 185.5) * mm});
            skArc(sketch, "E589", {"start": v(33.02, 186.18) * mm, "mid": v(33.2, 186.36) * mm, "end": v(33.27, 186.61) * mm});
            skLineSegment(sketch, "E590", {"start": v(33.27, 186.61) * mm, "end": v(33.27, 188.85) * mm});
            skLineSegment(sketch, "E591", {"start": v(33.27, 188.85) * mm, "end": v(-33.27, 188.85) * mm});
            skLineSegment(sketch, "E592", {"start": v(-33.27, 188.85) * mm, "end": v(-33.27, 186.61) * mm});
            skArc(sketch, "E593", {"start": v(-33.27, 186.61) * mm, "mid": v(-33.2, 186.36) * mm, "end": v(-33.02, 186.18) * mm});
            skArc(sketch, "E594", {"start": v(-33.7, 185.5) * mm, "mid": v(-32.91, 185.4) * mm, "end": v(-33.02, 186.18) * mm});
            skArc(sketch, "E595", {"start": v(-33.7, 185.5) * mm, "mid": v(-33.88, 185.68) * mm, "end": v(-34.13, 185.75) * mm});
            skLineSegment(sketch, "E596", {"start": v(-34.13, 185.75) * mm, "end": v(-40.9, 185.75) * mm});
            skLineSegment(sketch, "E597", {"start": v(-40.9, 185.75) * mm, "end": v(-40.9, 182.75) * mm});
            skLineSegment(sketch, "E598", {"start": v(-40.9, 182.75) * mm, "end": v(-39.63, 182.75) * mm});
            skLineSegment(sketch, "E599", {"start": v(-39.63, 182.75) * mm, "end": v(-39.63, 178.75) * mm});
            skLineSegment(sketch, "E600", {"start": v(-39.63, 178.75) * mm, "end": v(-40.9, 178.75) * mm});
            skLineSegment(sketch, "E601", {"start": v(-40.9, 178.75) * mm, "end": v(-40.9, 175.75) * mm});
            skLineSegment(sketch, "E602", {"start": v(-40.9, 175.75) * mm, "end": v(-44.1, 175.75) * mm});
            skLineSegment(sketch, "E603", {"start": v(-44.1, 175.75) * mm, "end": v(-44.1, 178.75) * mm});
            skLineSegment(sketch, "E604", {"start": v(-44.1, 178.75) * mm, "end": v(-45.38, 178.75) * mm});
            skLineSegment(sketch, "E605", {"start": v(-45.38, 178.75) * mm, "end": v(-45.38, 182.75) * mm});
            skLineSegment(sketch, "E606", {"start": v(-45.38, 182.75) * mm, "end": v(-44.1, 182.75) * mm});
            skLineSegment(sketch, "E607", {"start": v(-44.1, 182.75) * mm, "end": v(-44.1, 185.75) * mm});
            skLineSegment(sketch, "E608", {"start": v(-44.1, 185.75) * mm, "end": v(-50.88, 185.75) * mm});
            skArc(sketch, "E609", {"start": v(-50.88, 185.75) * mm, "mid": v(-51.13, 185.68) * mm, "end": v(-51.3, 185.5) * mm});
            skArc(sketch, "E610", {"start": v(-52, 186.18) * mm, "mid": v(-52.1, 185.4) * mm, "end": v(-51.3, 185.5) * mm});
            skArc(sketch, "E611", {"start": v(-52, 186.18) * mm, "mid": v(-51.8, 186.36) * mm, "end": v(-51.74, 186.61) * mm});
            skLineSegment(sketch, "E612", {"start": v(-51.74, 186.61) * mm, "end": v(-51.74, 188.85) * mm});
            skLineSegment(sketch, "E613", {"start": v(-51.74, 188.85) * mm, "end": v(-133.2, 188.85) * mm});
            skLineSegment(sketch, "E614", {"start": v(-133.2, 188.85) * mm, "end": v(-133.2, 186.61) * mm});
            skArc(sketch, "E615", {"start": v(-133.2, 186.61) * mm, "mid": v(-133.13, 186.36) * mm, "end": v(-132.95, 186.18) * mm});
            skArc(sketch, "E616", {"start": v(-133.63, 185.5) * mm, "mid": v(-132.85, 185.4) * mm, "end": v(-132.95, 186.18) * mm});
            skArc(sketch, "E617", {"start": v(-133.63, 185.5) * mm, "mid": v(-133.82, 185.68) * mm, "end": v(-134.07, 185.75) * mm});
            skLineSegment(sketch, "E618", {"start": v(-134.07, 185.75) * mm, "end": v(-157.57, 185.75) * mm});
            skLineSegment(sketch, "E619", {"start": v(-157.57, 185.75) * mm, "end": v(-157.57, 182.75) * mm});
            skLineSegment(sketch, "E620", {"start": v(-157.57, 182.75) * mm, "end": v(-156.3, 182.75) * mm});
            skLineSegment(sketch, "E621", {"start": v(-156.3, 182.75) * mm, "end": v(-156.3, 178.75) * mm});
            skLineSegment(sketch, "E622", {"start": v(-156.3, 178.75) * mm, "end": v(-157.57, 178.75) * mm});
            skLineSegment(sketch, "E623", {"start": v(-157.57, 178.75) * mm, "end": v(-157.57, 175.75) * mm});
            skLineSegment(sketch, "E624", {"start": v(-157.57, 175.75) * mm, "end": v(-160.78, 175.75) * mm});
            skLineSegment(sketch, "E625", {"start": v(-160.78, 175.75) * mm, "end": v(-160.78, 178.75) * mm});
            skLineSegment(sketch, "E626", {"start": v(-160.78, 178.75) * mm, "end": v(-162.05, 178.75) * mm});
            skLineSegment(sketch, "E627", {"start": v(-162.05, 178.75) * mm, "end": v(-162.05, 182.75) * mm});
            skLineSegment(sketch, "E628", {"start": v(-162.05, 182.75) * mm, "end": v(-160.78, 182.75) * mm});
            skLineSegment(sketch, "E629", {"start": v(-160.78, 182.75) * mm, "end": v(-160.78, 185.75) * mm});
            skLineSegment(sketch, "E630", {"start": v(-160.78, 185.75) * mm, "end": v(-184.13, 185.75) * mm});
            skArc(sketch, "E631", {"start": v(-184.13, 185.75) * mm, "mid": v(-184.38, 185.68) * mm, "end": v(-184.57, 185.5) * mm});
            skArc(sketch, "E632", {"start": v(-185.25, 186.18) * mm, "mid": v(-185.35, 185.4) * mm, "end": v(-184.57, 185.5) * mm});
            skArc(sketch, "E633", {"start": v(-185.25, 186.18) * mm, "mid": v(-185.07, 186.36) * mm, "end": v(-185, 186.61) * mm});
            skLineSegment(sketch, "E634", {"start": v(-185, 186.61) * mm, "end": v(-185, 188.85) * mm});
            skLineSegment(sketch, "E635", {"start": v(-185, 188.85) * mm, "end": v(-195, 188.85) * mm});
            skLineSegment(sketch, "E636", {"start": v(-195, 188.85) * mm, "end": v(-195, 179.33) * mm});
            skArc(sketch, "E637", {"start": v(-195, 179.33) * mm, "mid": v(-194.54, 177.04) * mm, "end": v(-193.24, 175.09) * mm});
            skLineSegment(sketch, "E638", {"start": v(-193.24, 175.09) * mm, "end": v(-188.76, 170.6) * mm});
            skArc(sketch, "E639", {"start": v(-187, 166.36) * mm, "mid": v(-187.46, 168.66) * mm, "end": v(-188.76, 170.6) * mm});
            skLineSegment(sketch, "E640", {"start": v(-187, 166.36) * mm, "end": v(-187, -114.67) * mm});
            skArc(sketch, "E641", {"start": v(-188.76, -118.91) * mm, "mid": v(-187.46, -116.96) * mm, "end": v(-187, -114.67) * mm});
            skLineSegment(sketch, "E642", {"start": v(-188.76, -118.91) * mm, "end": v(-193.24, -123.4) * mm});
            skArc(sketch, "E643", {"start": v(-193.24, -123.4) * mm, "mid": v(-194.54, -125.34) * mm, "end": v(-195, -127.64) * mm});
            skLineSegment(sketch, "E644", {"start": v(-195, -127.64) * mm, "end": v(-195, -176.15) * mm});
            skArc(sketch, "E645", {"start": v(-195, -176.15) * mm, "mid": v(-193.54, -179.69) * mm, "end": v(-190, -181.15) * mm});
            skLineSegment(sketch, "E646", {"start": v(-190, -181.15) * mm, "end": v(-100.41, -181.15) * mm});
            skArc(sketch, "E647", {"start": v(-100.41, -181.15) * mm, "mid": v(-100.03, -181.08) * mm, "end": v(-99.7, -180.86) * mm});
            skLineSegment(sketch, "E648", {"start": v(-99.7, -180.86) * mm, "end": v(-98.3, -179.45) * mm});
            skArc(sketch, "E649", {"start": v(-97.59, -179.15) * mm, "mid": v(-97.97, -179.23) * mm, "end": v(-98.3, -179.45) * mm});
            skLineSegment(sketch, "E650", {"start": v(-97.59, -179.15) * mm, "end": v(97.59, -179.15) * mm});
            skArc(sketch, "E651", {"start": v(98.3, -179.45) * mm, "mid": v(97.97, -179.23) * mm, "end": v(97.59, -179.15) * mm});
            skLineSegment(sketch, "E652", {"start": v(98.3, -179.45) * mm, "end": v(99.7, -180.86) * mm});
            skArc(sketch, "E653", {"start": v(99.7, -180.86) * mm, "mid": v(100.03, -181.08) * mm, "end": v(100.41, -181.15) * mm});
            skLineSegment(sketch, "E654", {"start": v(100.41, -181.15) * mm, "end": v(190, -181.15) * mm});
            skCircle(sketch, "E655", {"center": v(-189.82, -156.15) * mm, "radius": 1.6 * mm});
            skCircle(sketch, "E656", {"center": v(-140.78, -156.15) * mm, "radius": 1.6 * mm});
            skCircle(sketch, "E657", {"center": v(-120.18, 3.85) * mm, "radius": 1.6 * mm});
            skCircle(sketch, "E658", {"center": v(120.18, -116.15) * mm, "radius": 1.6 * mm});
            skCircle(sketch, "E659", {"center": v(120.17, 163.85) * mm, "radius": 1.6 * mm});
            skCircle(sketch, "E660", {"center": v(165.3, -129.5) * mm, "radius": 1.6 * mm});
            skCircle(sketch, "E661", {"center": v(-58.53, -156.15) * mm, "radius": 1.6 * mm});
            skLineSegment(sketch, "E662", {"start": v(44.83, -155.37) * mm, "end": v(44.83, -156.94) * mm});
            skArc(sketch, "E663", {"start": v(44.83, -155.37) * mm, "mid": v(44.76, -155.12) * mm, "end": v(44.58, -154.94) * mm});
            skArc(sketch, "E664", {"start": v(45.26, -154.25) * mm, "mid": v(44.47, -154.15) * mm, "end": v(44.58, -154.94) * mm});
            skArc(sketch, "E665", {"start": v(45.26, -154.25) * mm, "mid": v(45.44, -154.44) * mm, "end": v(45.7, -154.5) * mm});
            skLineSegment(sketch, "E666", {"start": v(50.16, -154.5) * mm, "end": v(45.7, -154.5) * mm});
            skArc(sketch, "E667", {"start": v(50.16, -154.5) * mm, "mid": v(50.4, -154.44) * mm, "end": v(50.6, -154.25) * mm});
            skArc(sketch, "E668", {"start": v(51.28, -154.94) * mm, "mid": v(51.38, -154.15) * mm, "end": v(50.6, -154.25) * mm});
            skArc(sketch, "E669", {"start": v(51.28, -154.94) * mm, "mid": v(51.1, -155.12) * mm, "end": v(51.03, -155.37) * mm});
            skLineSegment(sketch, "E670", {"start": v(51.03, -156.94) * mm, "end": v(51.03, -155.37) * mm});
            skArc(sketch, "E671", {"start": v(51.03, -156.94) * mm, "mid": v(51.1, -157.19) * mm, "end": v(51.28, -157.37) * mm});
            skArc(sketch, "E672", {"start": v(50.6, -158.05) * mm, "mid": v(51.38, -158.16) * mm, "end": v(51.28, -157.37) * mm});
            skArc(sketch, "E673", {"start": v(50.6, -158.05) * mm, "mid": v(50.4, -157.87) * mm, "end": v(50.16, -157.8) * mm});
            skLineSegment(sketch, "E674", {"start": v(45.7, -157.8) * mm, "end": v(50.16, -157.8) * mm});
            skArc(sketch, "E675", {"start": v(45.7, -157.8) * mm, "mid": v(45.44, -157.87) * mm, "end": v(45.26, -158.05) * mm});
            skArc(sketch, "E676", {"start": v(44.58, -157.37) * mm, "mid": v(44.47, -158.16) * mm, "end": v(45.26, -158.05) * mm});
            skArc(sketch, "E677", {"start": v(44.58, -157.37) * mm, "mid": v(44.76, -157.19) * mm, "end": v(44.83, -156.94) * mm});
            skLineSegment(sketch, "E678", {"start": v(66.03, -155.37) * mm, "end": v(66.03, -156.94) * mm});
            skArc(sketch, "E679", {"start": v(66.03, -155.37) * mm, "mid": v(65.96, -155.12) * mm, "end": v(65.78, -154.94) * mm});
            skArc(sketch, "E680", {"start": v(66.46, -154.25) * mm, "mid": v(65.67, -154.15) * mm, "end": v(65.78, -154.94) * mm});
            skArc(sketch, "E681", {"start": v(66.46, -154.25) * mm, "mid": v(66.64, -154.44) * mm, "end": v(66.9, -154.5) * mm});
            skLineSegment(sketch, "E682", {"start": v(71.36, -154.5) * mm, "end": v(66.9, -154.5) * mm});
            skArc(sketch, "E683", {"start": v(71.36, -154.5) * mm, "mid": v(71.6, -154.44) * mm, "end": v(71.8, -154.25) * mm});
            skArc(sketch, "E684", {"start": v(72.48, -154.94) * mm, "mid": v(72.58, -154.15) * mm, "end": v(71.8, -154.25) * mm});
            skArc(sketch, "E685", {"start": v(72.48, -154.94) * mm, "mid": v(72.3, -155.12) * mm, "end": v(72.23, -155.37) * mm});
            skLineSegment(sketch, "E686", {"start": v(72.23, -156.94) * mm, "end": v(72.23, -155.37) * mm});
            skArc(sketch, "E687", {"start": v(72.23, -156.94) * mm, "mid": v(72.3, -157.19) * mm, "end": v(72.48, -157.37) * mm});
            skArc(sketch, "E688", {"start": v(71.8, -158.05) * mm, "mid": v(72.58, -158.16) * mm, "end": v(72.48, -157.37) * mm});
            skArc(sketch, "E689", {"start": v(71.8, -158.05) * mm, "mid": v(71.6, -157.87) * mm, "end": v(71.36, -157.8) * mm});
            skLineSegment(sketch, "E690", {"start": v(66.9, -157.8) * mm, "end": v(71.36, -157.8) * mm});
            skArc(sketch, "E691", {"start": v(66.9, -157.8) * mm, "mid": v(66.64, -157.87) * mm, "end": v(66.46, -158.05) * mm});
            skArc(sketch, "E692", {"start": v(65.78, -157.37) * mm, "mid": v(65.67, -158.16) * mm, "end": v(66.46, -158.05) * mm});
            skArc(sketch, "E693", {"start": v(65.78, -157.37) * mm, "mid": v(65.96, -157.19) * mm, "end": v(66.03, -156.94) * mm});
            skCircle(sketch, "E694", {"center": v(79.02, -171.15) * mm, "radius": 1.6 * mm});
            skCircle(sketch, "E695", {"center": v(-39.5, -171.15) * mm, "radius": 1.6 * mm});
            skCircle(sketch, "E696", {"center": v(-165.3, -141.15) * mm, "radius": 1.6 * mm});
            skLineSegment(sketch, "E697", {"start": v(151.6, -140.37) * mm, "end": v(151.6, -141.94) * mm});
            skArc(sketch, "E698", {"start": v(151.6, -140.37) * mm, "mid": v(151.53, -140.12) * mm, "end": v(151.35, -139.94) * mm});
            skArc(sketch, "E699", {"start": v(152.03, -139.25) * mm, "mid": v(151.25, -139.15) * mm, "end": v(151.35, -139.94) * mm});
            skArc(sketch, "E700", {"start": v(152.03, -139.25) * mm, "mid": v(152.22, -139.44) * mm, "end": v(152.47, -139.5) * mm});
            skLineSegment(sketch, "E701", {"start": v(156.93, -139.5) * mm, "end": v(152.47, -139.5) * mm});
            skArc(sketch, "E702", {"start": v(156.93, -139.5) * mm, "mid": v(157.18, -139.44) * mm, "end": v(157.37, -139.25) * mm});
            skArc(sketch, "E703", {"start": v(158.05, -139.94) * mm, "mid": v(158.15, -139.15) * mm, "end": v(157.37, -139.25) * mm});
            skArc(sketch, "E704", {"start": v(158.05, -139.94) * mm, "mid": v(157.87, -140.12) * mm, "end": v(157.8, -140.37) * mm});
            skLineSegment(sketch, "E705", {"start": v(157.8, -141.94) * mm, "end": v(157.8, -140.37) * mm});
            skArc(sketch, "E706", {"start": v(157.8, -141.94) * mm, "mid": v(157.87, -142.19) * mm, "end": v(158.05, -142.37) * mm});
            skArc(sketch, "E707", {"start": v(157.37, -143.05) * mm, "mid": v(158.15, -143.16) * mm, "end": v(158.05, -142.37) * mm});
            skArc(sketch, "E708", {"start": v(157.37, -143.05) * mm, "mid": v(157.18, -142.87) * mm, "end": v(156.93, -142.8) * mm});
            skLineSegment(sketch, "E709", {"start": v(152.47, -142.8) * mm, "end": v(156.93, -142.8) * mm});
            skArc(sketch, "E710", {"start": v(152.47, -142.8) * mm, "mid": v(152.22, -142.87) * mm, "end": v(152.03, -143.05) * mm});
            skArc(sketch, "E711", {"start": v(151.35, -142.37) * mm, "mid": v(151.25, -143.16) * mm, "end": v(152.03, -143.05) * mm});
            skArc(sketch, "E712", {"start": v(151.35, -142.37) * mm, "mid": v(151.53, -142.19) * mm, "end": v(151.6, -141.94) * mm});
            skLineSegment(sketch, "E713", {"start": v(172.8, -140.37) * mm, "end": v(172.8, -141.94) * mm});
            skArc(sketch, "E714", {"start": v(172.8, -140.37) * mm, "mid": v(172.73, -140.12) * mm, "end": v(172.55, -139.94) * mm});
            skArc(sketch, "E715", {"start": v(173.23, -139.25) * mm, "mid": v(172.45, -139.15) * mm, "end": v(172.55, -139.94) * mm});
            skArc(sketch, "E716", {"start": v(173.23, -139.25) * mm, "mid": v(173.42, -139.44) * mm, "end": v(173.67, -139.5) * mm});
            skLineSegment(sketch, "E717", {"start": v(178.13, -139.5) * mm, "end": v(173.67, -139.5) * mm});
            skArc(sketch, "E718", {"start": v(178.13, -139.5) * mm, "mid": v(178.38, -139.44) * mm, "end": v(178.57, -139.25) * mm});
            skArc(sketch, "E719", {"start": v(179.25, -139.94) * mm, "mid": v(179.35, -139.15) * mm, "end": v(178.57, -139.25) * mm});
            skArc(sketch, "E720", {"start": v(179.25, -139.94) * mm, "mid": v(179.07, -140.12) * mm, "end": v(179, -140.37) * mm});
            skLineSegment(sketch, "E721", {"start": v(179, -141.94) * mm, "end": v(179, -140.37) * mm});
            skArc(sketch, "E722", {"start": v(179, -141.94) * mm, "mid": v(179.07, -142.19) * mm, "end": v(179.25, -142.37) * mm});
            skArc(sketch, "E723", {"start": v(178.57, -143.05) * mm, "mid": v(179.35, -143.16) * mm, "end": v(179.25, -142.37) * mm});
            skArc(sketch, "E724", {"start": v(178.57, -143.05) * mm, "mid": v(178.38, -142.87) * mm, "end": v(178.13, -142.8) * mm});
            skLineSegment(sketch, "E725", {"start": v(173.67, -142.8) * mm, "end": v(178.13, -142.8) * mm});
            skArc(sketch, "E726", {"start": v(173.67, -142.8) * mm, "mid": v(173.42, -142.87) * mm, "end": v(173.23, -143.05) * mm});
            skArc(sketch, "E727", {"start": v(172.55, -142.37) * mm, "mid": v(172.45, -143.16) * mm, "end": v(173.23, -143.05) * mm});
            skArc(sketch, "E728", {"start": v(172.55, -142.37) * mm, "mid": v(172.73, -142.19) * mm, "end": v(172.8, -141.94) * mm});
            skCircle(sketch, "E729", {"center": v(0, -171.15) * mm, "radius": 1.6 * mm});
            skLineSegment(sketch, "E730", {"start": v(136, -120.15) * mm, "end": v(136, -112.15) * mm});
            skArc(sketch, "E731", {"start": v(128, -120.15) * mm, "mid": v(132, -124.15) * mm, "end": v(136, -120.15) * mm});
            skLineSegment(sketch, "E732", {"start": v(128, -112.15) * mm, "end": v(128, -120.15) * mm});
            skArc(sketch, "E733", {"start": v(136, -112.15) * mm, "mid": v(132, -108.15) * mm, "end": v(128, -112.15) * mm});
            skLineSegment(sketch, "E734", {"start": v(172.2, -76.15) * mm, "end": v(172.2, -116.15) * mm});
            skArc(sketch, "E735", {"start": v(175.4, -76.15) * mm, "mid": v(173.8, -74.55) * mm, "end": v(172.2, -76.15) * mm});
            skLineSegment(sketch, "E736", {"start": v(175.4, -116.15) * mm, "end": v(175.4, -76.15) * mm});
            skArc(sketch, "E737", {"start": v(172.2, -116.15) * mm, "mid": v(173.8, -117.75) * mm, "end": v(175.4, -116.15) * mm});
            skLineSegment(sketch, "E738", {"start": v(153.2, -76.15) * mm, "end": v(153.2, -116.15) * mm});
            skArc(sketch, "E739", {"start": v(156.4, -76.15) * mm, "mid": v(154.8, -74.55) * mm, "end": v(153.2, -76.15) * mm});
            skLineSegment(sketch, "E740", {"start": v(156.4, -116.15) * mm, "end": v(156.4, -76.15) * mm});
            skArc(sketch, "E741", {"start": v(153.2, -116.15) * mm, "mid": v(154.8, -117.75) * mm, "end": v(156.4, -116.15) * mm});
            skLineSegment(sketch, "E742", {"start": v(162.7, -76.15) * mm, "end": v(162.7, -116.15) * mm});
            skArc(sketch, "E743", {"start": v(165.9, -76.15) * mm, "mid": v(164.3, -74.55) * mm, "end": v(162.7, -76.15) * mm});
            skLineSegment(sketch, "E744", {"start": v(165.9, -116.15) * mm, "end": v(165.9, -76.15) * mm});
            skArc(sketch, "E745", {"start": v(162.7, -116.15) * mm, "mid": v(164.3, -117.75) * mm, "end": v(165.9, -116.15) * mm});
            skLineSegment(sketch, "E746", {"start": v(174.5, 8.95) * mm, "end": v(169.5, 8.95) * mm});
            skArc(sketch, "E747", {"start": v(174.5, 5.75) * mm, "mid": v(176.1, 7.35) * mm, "end": v(174.5, 8.95) * mm});
            skLineSegment(sketch, "E748", {"start": v(169.5, 5.75) * mm, "end": v(174.5, 5.75) * mm});
            skArc(sketch, "E749", {"start": v(169.5, 8.95) * mm, "mid": v(167.9, 7.35) * mm, "end": v(169.5, 5.75) * mm});
            skLineSegment(sketch, "E750", {"start": v(-174.5, 5.75) * mm, "end": v(-169.5, 5.75) * mm});
            skArc(sketch, "E751", {"start": v(-174.5, 8.95) * mm, "mid": v(-176.1, 7.35) * mm, "end": v(-174.5, 5.75) * mm});
            skLineSegment(sketch, "E752", {"start": v(-169.5, 8.95) * mm, "end": v(-174.5, 8.95) * mm});
            skArc(sketch, "E753", {"start": v(-169.5, 5.75) * mm, "mid": v(-167.9, 7.35) * mm, "end": v(-169.5, 8.95) * mm});
            skLineSegment(sketch, "E754", {"start": v(-128, -120.15) * mm, "end": v(-128, -112.15) * mm});
            skArc(sketch, "E755", {"start": v(-136, -120.15) * mm, "mid": v(-132, -124.15) * mm, "end": v(-128, -120.15) * mm});
            skLineSegment(sketch, "E756", {"start": v(-136, -112.15) * mm, "end": v(-136, -120.15) * mm});
            skArc(sketch, "E757", {"start": v(-128, -112.15) * mm, "mid": v(-132, -108.15) * mm, "end": v(-136, -112.15) * mm});
            skLineSegment(sketch, "E758", {"start": v(-161, 75.98) * mm, "end": v(-138, 75.98) * mm});
            skArc(sketch, "E759", {"start": v(-165, 79.98) * mm, "mid": v(-163.83, 77.15) * mm, "end": v(-161, 75.98) * mm});
            skLineSegment(sketch, "E760", {"start": v(-165, 118.85) * mm, "end": v(-165, 79.98) * mm});
            skLineSegment(sketch, "E761", {"start": v(-164, 118.85) * mm, "end": v(-165, 118.85) * mm});
            skArc(sketch, "E762", {"start": v(-162, 116.85) * mm, "mid": v(-162.59, 118.26) * mm, "end": v(-164, 118.85) * mm});
            skLineSegment(sketch, "E763", {"start": v(-162, 79.98) * mm, "end": v(-162, 116.85) * mm});
            skArc(sketch, "E764", {"start": v(-162, 79.98) * mm, "mid": v(-161.7, 79.27) * mm, "end": v(-161, 78.98) * mm});
            skLineSegment(sketch, "E765", {"start": v(-138, 78.98) * mm, "end": v(-161, 78.98) * mm});
            skArc(sketch, "E766", {"start": v(-138, 78.98) * mm, "mid": v(-137.3, 79.27) * mm, "end": v(-137, 79.98) * mm});
            skLineSegment(sketch, "E767", {"start": v(-137, 93.98) * mm, "end": v(-137, 79.98) * mm});
            skLineSegment(sketch, "E768", {"start": v(-136, 93.98) * mm, "end": v(-137, 93.98) * mm});
            skArc(sketch, "E769", {"start": v(-134, 91.98) * mm, "mid": v(-134.59, 93.4) * mm, "end": v(-136, 93.98) * mm});
            skLineSegment(sketch, "E770", {"start": v(-134, 79.98) * mm, "end": v(-134, 91.98) * mm});
            skArc(sketch, "E771", {"start": v(-138, 75.98) * mm, "mid": v(-135.17, 77.15) * mm, "end": v(-134, 79.98) * mm});
            skLineSegment(sketch, "E772", {"start": v(-159, 96.98) * mm, "end": v(-159, 84.98) * mm});
            skArc(sketch, "E773", {"start": v(-155, 100.98) * mm, "mid": v(-157.83, 99.8) * mm, "end": v(-159, 96.98) * mm});
            skLineSegment(sketch, "E774", {"start": v(-132, 100.98) * mm, "end": v(-155, 100.98) * mm});
            skArc(sketch, "E775", {"start": v(-128, 96.98) * mm, "mid": v(-129.17, 99.8) * mm, "end": v(-132, 100.98) * mm});
            skLineSegment(sketch, "E776", {"start": v(-128, 62.98) * mm, "end": v(-128, 96.98) * mm});
            skArc(sketch, "E777", {"start": v(-132, 58.98) * mm, "mid": v(-129.17, 60.15) * mm, "end": v(-128, 62.98) * mm});
            skLineSegment(sketch, "E778", {"start": v(-151, 58.98) * mm, "end": v(-132, 58.98) * mm});
            skArc(sketch, "E779", {"start": v(-153, 60.98) * mm, "mid": v(-152.41, 59.57) * mm, "end": v(-151, 58.98) * mm});
            skLineSegment(sketch, "E780", {"start": v(-153, 61.98) * mm, "end": v(-153, 60.98) * mm});
            skLineSegment(sketch, "E781", {"start": v(-132, 61.98) * mm, "end": v(-153, 61.98) * mm});
            skArc(sketch, "E782", {"start": v(-132, 61.98) * mm, "mid": v(-131.3, 62.27) * mm, "end": v(-131, 62.98) * mm});
            skLineSegment(sketch, "E783", {"start": v(-131, 96.98) * mm, "end": v(-131, 62.98) * mm});
            skArc(sketch, "E784", {"start": v(-131, 96.98) * mm, "mid": v(-131.3, 97.69) * mm, "end": v(-132, 97.98) * mm});
            skLineSegment(sketch, "E785", {"start": v(-155, 97.98) * mm, "end": v(-132, 97.98) * mm});
            skArc(sketch, "E786", {"start": v(-155, 97.98) * mm, "mid": v(-155.7, 97.69) * mm, "end": v(-156, 96.98) * mm});
            skLineSegment(sketch, "E787", {"start": v(-156, 82.98) * mm, "end": v(-156, 96.98) * mm});
            skLineSegment(sketch, "E788", {"start": v(-157, 82.98) * mm, "end": v(-156, 82.98) * mm});
            skArc(sketch, "E789", {"start": v(-159, 84.98) * mm, "mid": v(-158.41, 83.57) * mm, "end": v(-157, 82.98) * mm});
            skLineSegment(sketch, "E790", {"start": v(-153, 91.98) * mm, "end": v(-144, 91.98) * mm});
            skArc(sketch, "E791", {"start": v(-150, 94.98) * mm, "mid": v(-152.12, 94.1) * mm, "end": v(-153, 91.98) * mm});
            skLineSegment(sketch, "E792", {"start": v(-143, 94.98) * mm, "end": v(-150, 94.98) * mm});
            skArc(sketch, "E793", {"start": v(-140, 91.98) * mm, "mid": v(-140.88, 94.1) * mm, "end": v(-143, 94.98) * mm});
            skLineSegment(sketch, "E794", {"start": v(-140, 86.98) * mm, "end": v(-140, 91.98) * mm});
            skLineSegment(sketch, "E795", {"start": v(-143, 86.98) * mm, "end": v(-140, 86.98) * mm});
            skLineSegment(sketch, "E796", {"start": v(-143, 90.98) * mm, "end": v(-143, 86.98) * mm});
            skArc(sketch, "E797", {"start": v(-143, 90.98) * mm, "mid": v(-143.3, 91.69) * mm, "end": v(-144, 91.98) * mm});
            skLineSegment(sketch, "E798", {"start": v(-140, 84.98) * mm, "end": v(-149, 84.98) * mm});
            skArc(sketch, "E799", {"start": v(-143, 81.98) * mm, "mid": v(-140.88, 82.86) * mm, "end": v(-140, 84.98) * mm});
            skLineSegment(sketch, "E800", {"start": v(-150, 81.98) * mm, "end": v(-143, 81.98) * mm});
            skArc(sketch, "E801", {"start": v(-153, 84.98) * mm, "mid": v(-152.12, 82.86) * mm, "end": v(-150, 81.98) * mm});
            skLineSegment(sketch, "E802", {"start": v(-153, 89.98) * mm, "end": v(-153, 84.98) * mm});
            skLineSegment(sketch, "E803", {"start": v(-150, 89.98) * mm, "end": v(-153, 89.98) * mm});
            skLineSegment(sketch, "E804", {"start": v(-150, 85.98) * mm, "end": v(-150, 89.98) * mm});
            skArc(sketch, "E805", {"start": v(-150, 85.98) * mm, "mid": v(-149.7, 85.27) * mm, "end": v(-149, 84.98) * mm});
            skCircle(sketch, "E806", {"center": v(-80, 158.85) * mm, "radius": 1.6 * mm});
            skCircle(sketch, "E807", {"center": v(80, 158.85) * mm, "radius": 1.6 * mm});
            skCircle(sketch, "E808", {"center": v(180, -171.15) * mm, "radius": 1.6 * mm});
            skLineSegment(sketch, "E809", {"start": v(175.82, 160.75) * mm, "end": v(175.82, 170.75) * mm});
            skLineSegment(sketch, "E810", {"start": v(171.82, 160.75) * mm, "end": v(175.82, 160.75) * mm});
            skLineSegment(sketch, "E811", {"start": v(171.82, 170.75) * mm, "end": v(171.82, 160.75) * mm});
            skLineSegment(sketch, "E812", {"start": v(175.82, 170.75) * mm, "end": v(171.82, 170.75) * mm});
            skLineSegment(sketch, "E813", {"start": v(175.82, 135.75) * mm, "end": v(175.82, 145.75) * mm});
            skLineSegment(sketch, "E814", {"start": v(171.82, 135.75) * mm, "end": v(175.82, 135.75) * mm});
            skLineSegment(sketch, "E815", {"start": v(171.82, 145.75) * mm, "end": v(171.82, 135.75) * mm});
            skLineSegment(sketch, "E816", {"start": v(175.82, 145.75) * mm, "end": v(171.82, 145.75) * mm});
            skSolve(sketch);
        }
        {
            var Q0;
            Q0 = qSketchRegion(id + "F0", true);
            extrude(context, id + "F1", {"entities" : qUnion([Q0]), "depth" : 3 * mm, "offsetDistance" : 25 * mm});
        }
    });
